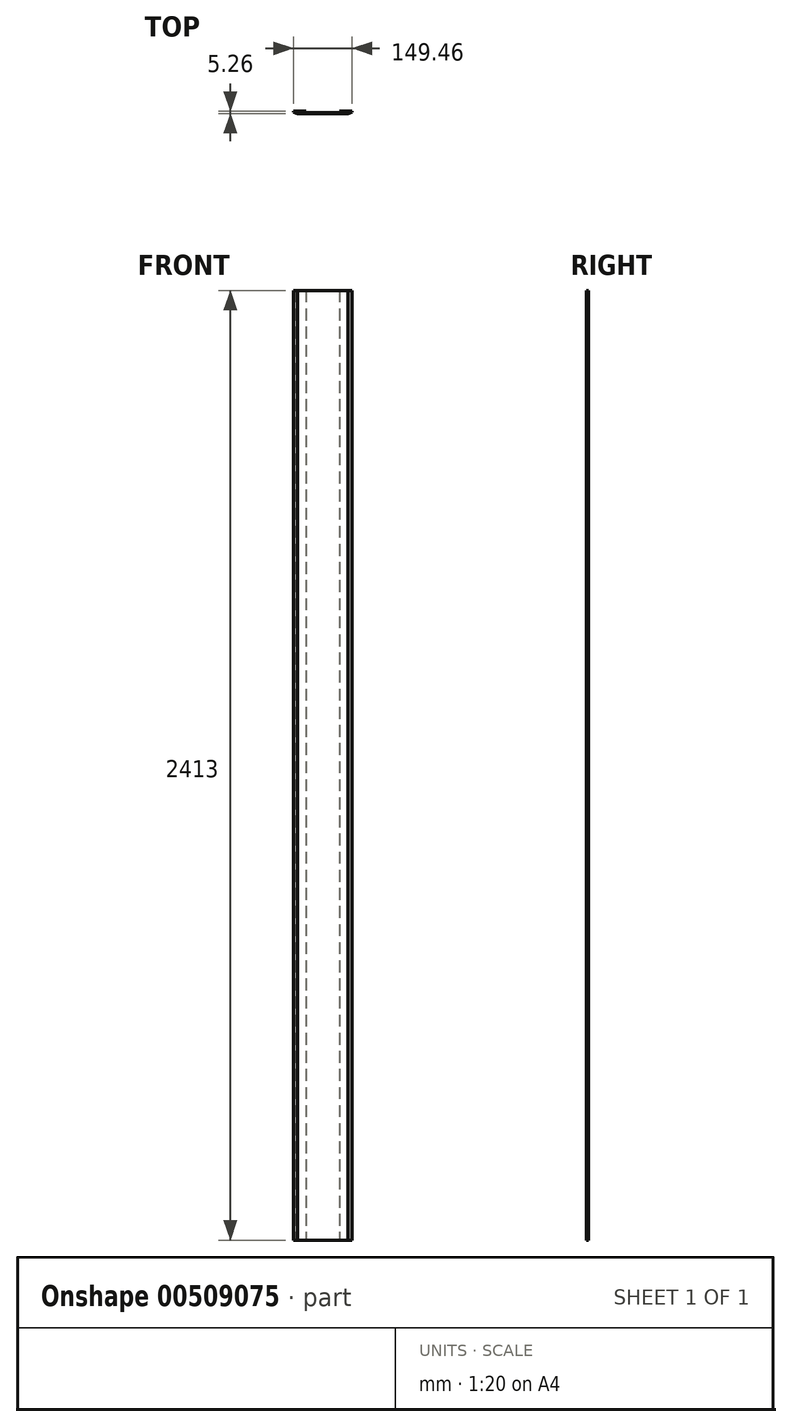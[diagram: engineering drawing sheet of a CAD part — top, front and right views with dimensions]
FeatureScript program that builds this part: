
annotation { "Feature Type Name" : "Feature", "Feature Type Description" : "" }
export const myFeature = defineFeature(function(context is Context, id is Id, definition is map)
    precondition{}
    {
        {
            var Q0;
            Q0=qCreatedBy(makeId("Top.planeOp"),FACE);
            var sketch = newSketch(context, id + "F0", { "sketchPlane" : qUnion([Q0])});
            skLineSegment(sketch, "E0", {"start": v(-431.8, -558.8) * mm, "end": v(431.8, -558.8) * mm});
            skLineSegment(sketch, "E1", {"start": v(431.8, -558.8) * mm, "end": v(431.8, 558.8) * mm});
            skLineSegment(sketch, "E2", {"start": v(431.8, 558.8) * mm, "end": v(-431.8, 558.8) * mm});
            skLineSegment(sketch, "E3", {"start": v(-431.8, 558.8) * mm, "end": v(-431.8, -558.8) * mm});
            skLineSegment(sketch, "E4", {"start": v(-381, -504.83) * mm, "end": v(381, -504.83) * mm});
            skLineSegment(sketch, "E5", {"start": v(381, -504.83) * mm, "end": v(381, 504.83) * mm});
            skLineSegment(sketch, "E6", {"start": v(381, 504.83) * mm, "end": v(360.7, 504.83) * mm});
            skLineSegment(sketch, "E7", {"start": v(265.82, 504.83) * mm, "end": v(-381, 504.83) * mm});
            skLineSegment(sketch, "E8", {"start": v(-381, 504.83) * mm, "end": v(-381, -504.83) * mm});
            skLineSegment(sketch, "E9", {"start": v(-381, -403.23) * mm, "end": v(381, -403.23) * mm});
            skLineSegment(sketch, "E10", {"start": v(-152.4, -403.23) * mm, "end": v(-152.4, -504.83) * mm});
            skLineSegment(sketch, "E11", {"start": v(152.4, -403.23) * mm, "end": v(152.4, -504.83) * mm});
            skLineSegment(sketch, "E12", {"start": v(349.12, 503.33) * mm, "end": v(324.77, 544.8) * mm});
            skLineSegment(sketch, "E13", {"start": v(324.92, 525.17) * mm, "end": v(343.26, 493.25) * mm});
            skLineSegment(sketch, "E14", {"start": v(345.3, 496.77) * mm, "end": v(323.11, 534.57) * mm});
            skLineSegment(sketch, "E15", {"start": v(351.17, 506.85) * mm, "end": v(327.06, 548.5) * mm});
            skLineSegment(sketch, "E16", {"start": v(335.24, 486.66) * mm, "end": v(339.43, 486.66) * mm});
            skLineSegment(sketch, "E17", {"start": v(323.53, 514.34) * mm, "end": v(339.43, 486.66) * mm});
            skLineSegment(sketch, "E18", {"start": v(324.77, 544.8) * mm, "end": v(303.2, 507.27) * mm});
            skLineSegment(sketch, "E19", {"start": v(323.11, 534.57) * mm, "end": v(305.2, 503.47) * mm});
            skLineSegment(sketch, "E20", {"start": v(303.02, 548.5) * mm, "end": v(279.32, 507.27) * mm});
            skLineSegment(sketch, "E21", {"start": v(305.2, 503.47) * mm, "end": v(281.51, 503.47) * mm});
            skLineSegment(sketch, "E22", {"start": v(303.2, 507.27) * mm, "end": v(279.32, 507.27) * mm});
            skLineSegment(sketch, "E23", {"start": v(287.46, 493.17) * mm, "end": v(311.53, 493.17) * mm});
            skLineSegment(sketch, "E24", {"start": v(285.48, 496.6) * mm, "end": v(309, 496.6) * mm});
            skLineSegment(sketch, "E25", {"start": v(315.3, 486.66) * mm, "end": v(291.22, 486.66) * mm});
            skLineSegment(sketch, "E26", {"start": v(281.51, 503.47) * mm, "end": v(285.48, 496.6) * mm});
            skLineSegment(sketch, "E27", {"start": v(287.46, 493.17) * mm, "end": v(291.22, 486.66) * mm});
            skLineSegment(sketch, "E28", {"start": v(309, 496.6) * mm, "end": v(324.92, 525.17) * mm});
            skLineSegment(sketch, "E29", {"start": v(311.53, 493.17) * mm, "end": v(323.53, 514.34) * mm});
            skLineSegment(sketch, "E30", {"start": v(325.28, 503.65) * mm, "end": v(315.3, 486.66) * mm});
            skLineSegment(sketch, "E31", {"start": v(319.7, 486.66) * mm, "end": v(326.89, 486.66) * mm});
            skLineSegment(sketch, "E32", {"start": v(319.7, 486.66) * mm, "end": v(323.3, 492.99) * mm});
            skLineSegment(sketch, "E33", {"start": v(335.24, 486.66) * mm, "end": v(325.28, 503.65) * mm});
            skLineSegment(sketch, "E34", {"start": v(323.3, 492.99) * mm, "end": v(326.89, 486.66) * mm});
            skLineSegment(sketch, "E35", {"start": v(327.06, 548.5) * mm, "end": v(303.02, 548.5) * mm});
            skLineSegment(sketch, "E36", {"start": v(343.26, 493.25) * mm, "end": v(345.3, 496.77) * mm});
            skLineSegment(sketch, "E37", {"start": v(349.12, 503.33) * mm, "end": v(351.17, 506.85) * mm});
            skCircle(sketch, "E38", {"center": v(350.6, 458.79) * mm, "radius": 1.85 * mm});
            skLineSegment(sketch, "E39", {"start": v(-201.65, 389.86) * mm, "end": v(-204.7, 389.86) * mm});
            skLineSegment(sketch, "E40", {"start": v(-201.65, 287.56) * mm, "end": v(-204.7, 287.56) * mm});
            skLineSegment(sketch, "E41", {"start": v(-204.7, 389.86) * mm, "end": v(-204.7, 405.1) * mm});
            skLineSegment(sketch, "E42", {"start": v(-201.65, 389.86) * mm, "end": v(-201.65, 405.1) * mm});
            skArc(sketch, "E43", {"start": v(-200.89, 405.86) * mm, "mid": v(-201.43, 405.64) * mm, "end": v(-201.65, 405.1) * mm});
            skArc(sketch, "E44", {"start": v(-200.89, 408.9) * mm, "mid": v(-203.58, 407.8) * mm, "end": v(-204.7, 405.1) * mm});
            skLineSegment(sketch, "E45", {"start": v(-200.89, 408.9) * mm, "end": v(-151.83, 408.9) * mm});
            skLineSegment(sketch, "E46", {"start": v(-200.89, 405.86) * mm, "end": v(-151.83, 405.86) * mm});
            skArc(sketch, "E47", {"start": v(-151.07, 405.1) * mm, "mid": v(-151.3, 405.64) * mm, "end": v(-151.83, 405.86) * mm});
            skArc(sketch, "E48", {"start": v(-148.02, 405.1) * mm, "mid": v(-149.14, 407.8) * mm, "end": v(-151.83, 408.9) * mm});
            skLineSegment(sketch, "E49", {"start": v(-148.02, 405.1) * mm, "end": v(-148.02, 272.32) * mm});
            skLineSegment(sketch, "E50", {"start": v(-151.07, 405.1) * mm, "end": v(-151.07, 272.32) * mm});
            skLineSegment(sketch, "E51", {"start": v(-204.7, 287.56) * mm, "end": v(-204.7, 273.15) * mm});
            skLineSegment(sketch, "E52", {"start": v(-201.65, 287.56) * mm, "end": v(-201.65, 273.15) * mm});
            skLineSegment(sketch, "E53", {"start": v(-200.06, 268.51) * mm, "end": v(-151.83, 268.51) * mm});
            skLineSegment(sketch, "E54", {"start": v(-200.06, 271.56) * mm, "end": v(-151.83, 271.56) * mm});
            skArc(sketch, "E55", {"start": v(-151.83, 271.56) * mm, "mid": v(-151.3, 271.79) * mm, "end": v(-151.07, 272.32) * mm});
            skArc(sketch, "E56", {"start": v(-151.83, 268.51) * mm, "mid": v(-149.14, 269.63) * mm, "end": v(-148.02, 272.32) * mm});
            skArc(sketch, "E57", {"start": v(-201.65, 273.15) * mm, "mid": v(-201.19, 272.03) * mm, "end": v(-200.06, 271.56) * mm});
            skArc(sketch, "E58", {"start": v(-204.7, 273.15) * mm, "mid": v(-203.34, 269.87) * mm, "end": v(-200.06, 268.51) * mm});
            skLineSegment(sketch, "E59", {"start": v(268.24, 192.18) * mm, "end": v(-275.4, 192.18) * mm});
            skLineSegment(sketch, "E60", {"start": v(-275.4, 267.58) * mm, "end": v(268.24, 267.58) * mm});
            skLineSegment(sketch, "E61", {"start": v(-275.4, 191.38) * mm, "end": v(268.24, 191.38) * mm});
            skLineSegment(sketch, "E62", {"start": v(-275.4, 189.56) * mm, "end": v(-275.4, 233.5) * mm});
            skLineSegment(sketch, "E63", {"start": v(-275.4, 238.46) * mm, "end": v(-275.4, 270.12) * mm});
            skLineSegment(sketch, "E64", {"start": v(-275.4, 233.5) * mm, "end": v(-264.27, 236) * mm});
            skLineSegment(sketch, "E65", {"start": v(-287.59, 236) * mm, "end": v(-275.4, 238.46) * mm});
            skLineSegment(sketch, "E66", {"start": v(-287.59, 236) * mm, "end": v(-264.27, 236) * mm});
            skLineSegment(sketch, "E67", {"start": v(268.24, 189.56) * mm, "end": v(268.24, 233.5) * mm});
            skLineSegment(sketch, "E68", {"start": v(268.24, 238.46) * mm, "end": v(268.24, 270.12) * mm});
            skLineSegment(sketch, "E69", {"start": v(268.24, 233.5) * mm, "end": v(279.38, 236) * mm});
            skLineSegment(sketch, "E70", {"start": v(256.06, 236) * mm, "end": v(268.24, 238.46) * mm});
            skLineSegment(sketch, "E71", {"start": v(256.06, 236) * mm, "end": v(279.38, 236) * mm});
            skLineSegment(sketch, "E72", {"start": v(267.92, 175.66) * mm, "end": v(267.92, 187.92) * mm});
            skLineSegment(sketch, "E73", {"start": v(-275.4, 175.66) * mm, "end": v(-275.4, 187.92) * mm});
            skLineSegment(sketch, "E74", {"start": v(131.2, 389.86) * mm, "end": v(128.15, 389.86) * mm});
            skLineSegment(sketch, "E75", {"start": v(131.2, 287.54) * mm, "end": v(128.15, 287.54) * mm});
            skLineSegment(sketch, "E76", {"start": v(128.15, 389.86) * mm, "end": v(128.15, 405.1) * mm});
            skLineSegment(sketch, "E77", {"start": v(131.2, 389.86) * mm, "end": v(131.2, 405.1) * mm});
            skArc(sketch, "E78", {"start": v(131.96, 408.9) * mm, "mid": v(129.27, 407.8) * mm, "end": v(128.15, 405.1) * mm});
            skLineSegment(sketch, "E79", {"start": v(131.96, 408.9) * mm, "end": v(182.96, 408.9) * mm});
            skLineSegment(sketch, "E80", {"start": v(131.96, 405.86) * mm, "end": v(182.96, 405.86) * mm});
            skArc(sketch, "E81", {"start": v(183.72, 405.1) * mm, "mid": v(183.5, 405.64) * mm, "end": v(182.96, 405.86) * mm});
            skArc(sketch, "E82", {"start": v(186.77, 405.1) * mm, "mid": v(185.65, 407.8) * mm, "end": v(182.96, 408.9) * mm});
            skLineSegment(sketch, "E83", {"start": v(186.77, 405.1) * mm, "end": v(186.77, 272.3) * mm});
            skLineSegment(sketch, "E84", {"start": v(183.72, 405.1) * mm, "end": v(183.72, 272.3) * mm});
            skLineSegment(sketch, "E85", {"start": v(128.15, 287.54) * mm, "end": v(128.15, 273.12) * mm});
            skLineSegment(sketch, "E86", {"start": v(131.2, 287.54) * mm, "end": v(131.2, 273.12) * mm});
            skLineSegment(sketch, "E87", {"start": v(132.79, 268.49) * mm, "end": v(182.96, 268.49) * mm});
            skLineSegment(sketch, "E88", {"start": v(132.79, 271.53) * mm, "end": v(182.96, 271.53) * mm});
            skArc(sketch, "E89", {"start": v(182.96, 271.53) * mm, "mid": v(183.5, 271.76) * mm, "end": v(183.72, 272.3) * mm});
            skArc(sketch, "E90", {"start": v(182.96, 268.49) * mm, "mid": v(185.65, 269.6) * mm, "end": v(186.77, 272.3) * mm});
            skArc(sketch, "E91", {"start": v(131.2, 273.12) * mm, "mid": v(131.67, 272) * mm, "end": v(132.79, 271.53) * mm});
            skArc(sketch, "E92", {"start": v(128.15, 273.12) * mm, "mid": v(129.51, 269.84) * mm, "end": v(132.79, 268.49) * mm});
            skLineSegment(sketch, "E93", {"start": v(-275.4, 266.78) * mm, "end": v(268.24, 266.78) * mm});
            skArc(sketch, "E94", {"start": v(131.96, 405.86) * mm, "mid": v(131.42, 405.64) * mm, "end": v(131.2, 405.1) * mm});
            skLineSegment(sketch, "E95", {"start": v(-148.02, 350.55) * mm, "end": v(-147.38, 350.55) * mm});
            skLineSegment(sketch, "E96", {"start": v(268.24, 220.63) * mm, "end": v(-275.4, 220.63) * mm});
            skLineSegment(sketch, "E97", {"start": v(-275.4, 219.83) * mm, "end": v(268.24, 219.83) * mm});
            skLineSegment(sketch, "E98", {"start": v(111.4, 219.88) * mm, "end": v(200.2, 219.88) * mm});
            skLineSegment(sketch, "E99", {"start": v(200.2, 219.88) * mm, "end": v(200.2, 218.1) * mm});
            skLineSegment(sketch, "E100", {"start": v(111.4, 219.88) * mm, "end": v(111.4, 218.1) * mm});
            skLineSegment(sketch, "E101", {"start": v(111.4, 218.1) * mm, "end": v(200.2, 218.1) * mm});
            skLineSegment(sketch, "E102", {"start": v(165.87, 216.24) * mm, "end": v(165.87, 217.5) * mm});
            skLineSegment(sketch, "E103", {"start": v(152.66, 216.24) * mm, "end": v(152.66, 217.5) * mm});
            skLineSegment(sketch, "E104", {"start": v(164.46, 211.81) * mm, "end": v(164.46, 216.24) * mm});
            skLineSegment(sketch, "E105", {"start": v(154.07, 211.81) * mm, "end": v(154.07, 216.24) * mm});
            skLineSegment(sketch, "E106", {"start": v(161.7, 259.32) * mm, "end": v(161.7, 260.34) * mm});
            skLineSegment(sketch, "E107", {"start": v(161.7, 261.14) * mm, "end": v(161.7, 262.16) * mm});
            skLineSegment(sketch, "E108", {"start": v(161.7, 262.95) * mm, "end": v(161.7, 263.97) * mm});
            skLineSegment(sketch, "E109", {"start": v(161.7, 264.76) * mm, "end": v(161.7, 265.78) * mm});
            skLineSegment(sketch, "E110", {"start": v(161.7, 266.58) * mm, "end": v(161.7, 267.6) * mm});
            skLineSegment(sketch, "E111", {"start": v(161.7, 268.39) * mm, "end": v(161.7, 269.41) * mm});
            skLineSegment(sketch, "E112", {"start": v(161.7, 270.2) * mm, "end": v(161.7, 271.22) * mm});
            skLineSegment(sketch, "E113", {"start": v(161.7, 272.02) * mm, "end": v(161.7, 273.04) * mm});
            skLineSegment(sketch, "E114", {"start": v(161.7, 273.83) * mm, "end": v(161.7, 274.85) * mm});
            skLineSegment(sketch, "E115", {"start": v(161.7, 275.64) * mm, "end": v(161.7, 276.67) * mm});
            skLineSegment(sketch, "E116", {"start": v(161.7, 277.46) * mm, "end": v(161.7, 278.48) * mm});
            skLineSegment(sketch, "E117", {"start": v(156.83, 257.5) * mm, "end": v(156.83, 258.53) * mm});
            skLineSegment(sketch, "E118", {"start": v(156.83, 259.32) * mm, "end": v(156.83, 260.34) * mm});
            skLineSegment(sketch, "E119", {"start": v(156.83, 261.14) * mm, "end": v(156.83, 262.16) * mm});
            skLineSegment(sketch, "E120", {"start": v(156.83, 262.95) * mm, "end": v(156.83, 263.97) * mm});
            skLineSegment(sketch, "E121", {"start": v(156.83, 264.76) * mm, "end": v(156.83, 265.78) * mm});
            skLineSegment(sketch, "E122", {"start": v(156.83, 266.58) * mm, "end": v(156.83, 267.6) * mm});
            skLineSegment(sketch, "E123", {"start": v(156.83, 268.39) * mm, "end": v(156.83, 269.41) * mm});
            skLineSegment(sketch, "E124", {"start": v(156.83, 270.2) * mm, "end": v(156.83, 271.22) * mm});
            skLineSegment(sketch, "E125", {"start": v(156.83, 272.02) * mm, "end": v(156.83, 273.04) * mm});
            skLineSegment(sketch, "E126", {"start": v(156.83, 273.83) * mm, "end": v(156.83, 274.85) * mm});
            skLineSegment(sketch, "E127", {"start": v(156.83, 275.64) * mm, "end": v(156.83, 276.67) * mm});
            skLineSegment(sketch, "E128", {"start": v(156.14, 258.93) * mm, "end": v(156.83, 258.53) * mm});
            skLineSegment(sketch, "E129", {"start": v(156.14, 258.93) * mm, "end": v(156.83, 259.32) * mm});
            skLineSegment(sketch, "E130", {"start": v(156.14, 260.74) * mm, "end": v(156.83, 260.34) * mm});
            skLineSegment(sketch, "E131", {"start": v(156.14, 260.74) * mm, "end": v(156.83, 261.14) * mm});
            skLineSegment(sketch, "E132", {"start": v(162.39, 260.74) * mm, "end": v(161.7, 260.34) * mm});
            skLineSegment(sketch, "E133", {"start": v(162.39, 260.74) * mm, "end": v(161.7, 261.14) * mm});
            skLineSegment(sketch, "E134", {"start": v(162.39, 262.55) * mm, "end": v(161.7, 262.16) * mm});
            skLineSegment(sketch, "E135", {"start": v(162.39, 262.55) * mm, "end": v(161.7, 262.95) * mm});
            skLineSegment(sketch, "E136", {"start": v(156.14, 258.93) * mm, "end": v(162.39, 260.74) * mm});
            skLineSegment(sketch, "E137", {"start": v(156.14, 260.74) * mm, "end": v(162.39, 262.55) * mm});
            skLineSegment(sketch, "E138", {"start": v(156.83, 258.53) * mm, "end": v(161.7, 260.34) * mm});
            skLineSegment(sketch, "E139", {"start": v(156.83, 259.32) * mm, "end": v(161.7, 261.14) * mm});
            skLineSegment(sketch, "E140", {"start": v(156.83, 260.34) * mm, "end": v(161.7, 262.16) * mm});
            skLineSegment(sketch, "E141", {"start": v(156.83, 261.14) * mm, "end": v(161.7, 262.95) * mm});
            skLineSegment(sketch, "E142", {"start": v(156.14, 262.55) * mm, "end": v(156.83, 262.16) * mm});
            skLineSegment(sketch, "E143", {"start": v(156.14, 262.55) * mm, "end": v(156.83, 262.95) * mm});
            skLineSegment(sketch, "E144", {"start": v(156.14, 264.37) * mm, "end": v(156.83, 263.97) * mm});
            skLineSegment(sketch, "E145", {"start": v(156.14, 264.37) * mm, "end": v(156.83, 264.76) * mm});
            skLineSegment(sketch, "E146", {"start": v(162.39, 264.37) * mm, "end": v(161.7, 263.97) * mm});
            skLineSegment(sketch, "E147", {"start": v(162.39, 264.37) * mm, "end": v(161.7, 264.76) * mm});
            skLineSegment(sketch, "E148", {"start": v(162.39, 266.18) * mm, "end": v(161.7, 265.78) * mm});
            skLineSegment(sketch, "E149", {"start": v(162.39, 266.18) * mm, "end": v(161.7, 266.58) * mm});
            skLineSegment(sketch, "E150", {"start": v(156.14, 262.55) * mm, "end": v(162.39, 264.37) * mm});
            skLineSegment(sketch, "E151", {"start": v(156.14, 264.37) * mm, "end": v(162.39, 266.18) * mm});
            skLineSegment(sketch, "E152", {"start": v(156.83, 262.16) * mm, "end": v(161.7, 263.97) * mm});
            skLineSegment(sketch, "E153", {"start": v(156.83, 262.95) * mm, "end": v(161.7, 264.76) * mm});
            skLineSegment(sketch, "E154", {"start": v(156.83, 263.97) * mm, "end": v(161.7, 265.78) * mm});
            skLineSegment(sketch, "E155", {"start": v(156.83, 264.76) * mm, "end": v(161.7, 266.58) * mm});
            skLineSegment(sketch, "E156", {"start": v(156.14, 266.18) * mm, "end": v(156.83, 265.78) * mm});
            skLineSegment(sketch, "E157", {"start": v(156.14, 266.18) * mm, "end": v(156.83, 266.58) * mm});
            skLineSegment(sketch, "E158", {"start": v(162.39, 268) * mm, "end": v(161.7, 267.6) * mm});
            skLineSegment(sketch, "E159", {"start": v(162.39, 268) * mm, "end": v(161.7, 268.39) * mm});
            skLineSegment(sketch, "E160", {"start": v(156.14, 266.18) * mm, "end": v(162.39, 268) * mm});
            skLineSegment(sketch, "E161", {"start": v(156.83, 265.78) * mm, "end": v(161.7, 267.6) * mm});
            skLineSegment(sketch, "E162", {"start": v(156.83, 266.58) * mm, "end": v(161.7, 268.39) * mm});
            skLineSegment(sketch, "E163", {"start": v(156.14, 268) * mm, "end": v(156.83, 267.6) * mm});
            skLineSegment(sketch, "E164", {"start": v(156.14, 268) * mm, "end": v(156.83, 268.39) * mm});
            skLineSegment(sketch, "E165", {"start": v(156.14, 269.8) * mm, "end": v(156.83, 269.41) * mm});
            skLineSegment(sketch, "E166", {"start": v(156.14, 269.8) * mm, "end": v(156.83, 270.2) * mm});
            skLineSegment(sketch, "E167", {"start": v(162.39, 269.8) * mm, "end": v(161.7, 269.41) * mm});
            skLineSegment(sketch, "E168", {"start": v(162.39, 269.8) * mm, "end": v(161.7, 270.2) * mm});
            skLineSegment(sketch, "E169", {"start": v(162.39, 271.62) * mm, "end": v(161.7, 271.22) * mm});
            skLineSegment(sketch, "E170", {"start": v(162.39, 271.62) * mm, "end": v(161.7, 272.02) * mm});
            skLineSegment(sketch, "E171", {"start": v(156.14, 268) * mm, "end": v(162.39, 269.8) * mm});
            skLineSegment(sketch, "E172", {"start": v(156.14, 269.8) * mm, "end": v(162.39, 271.62) * mm});
            skLineSegment(sketch, "E173", {"start": v(156.83, 267.6) * mm, "end": v(161.7, 269.41) * mm});
            skLineSegment(sketch, "E174", {"start": v(156.83, 268.39) * mm, "end": v(161.7, 270.2) * mm});
            skLineSegment(sketch, "E175", {"start": v(156.83, 269.41) * mm, "end": v(161.7, 271.22) * mm});
            skLineSegment(sketch, "E176", {"start": v(156.83, 270.2) * mm, "end": v(161.7, 272.02) * mm});
            skLineSegment(sketch, "E177", {"start": v(156.14, 271.62) * mm, "end": v(156.83, 271.22) * mm});
            skLineSegment(sketch, "E178", {"start": v(156.14, 271.62) * mm, "end": v(156.83, 272.02) * mm});
            skLineSegment(sketch, "E179", {"start": v(156.14, 273.43) * mm, "end": v(156.83, 273.04) * mm});
            skLineSegment(sketch, "E180", {"start": v(156.14, 273.43) * mm, "end": v(156.83, 273.83) * mm});
            skLineSegment(sketch, "E181", {"start": v(162.39, 273.43) * mm, "end": v(161.7, 273.04) * mm});
            skLineSegment(sketch, "E182", {"start": v(162.39, 273.43) * mm, "end": v(161.7, 273.83) * mm});
            skLineSegment(sketch, "E183", {"start": v(162.39, 275.25) * mm, "end": v(161.7, 274.85) * mm});
            skLineSegment(sketch, "E184", {"start": v(162.39, 275.25) * mm, "end": v(161.7, 275.64) * mm});
            skLineSegment(sketch, "E185", {"start": v(156.14, 271.62) * mm, "end": v(162.39, 273.43) * mm});
            skLineSegment(sketch, "E186", {"start": v(156.14, 273.43) * mm, "end": v(162.39, 275.25) * mm});
            skLineSegment(sketch, "E187", {"start": v(156.83, 271.22) * mm, "end": v(161.7, 273.04) * mm});
            skLineSegment(sketch, "E188", {"start": v(156.83, 272.02) * mm, "end": v(161.7, 273.83) * mm});
            skLineSegment(sketch, "E189", {"start": v(156.83, 273.04) * mm, "end": v(161.7, 274.85) * mm});
            skLineSegment(sketch, "E190", {"start": v(156.83, 273.83) * mm, "end": v(161.7, 275.64) * mm});
            skLineSegment(sketch, "E191", {"start": v(156.14, 275.25) * mm, "end": v(156.83, 274.85) * mm});
            skLineSegment(sketch, "E192", {"start": v(156.14, 275.25) * mm, "end": v(156.83, 275.64) * mm});
            skLineSegment(sketch, "E193", {"start": v(156.14, 277.06) * mm, "end": v(156.83, 276.67) * mm});
            skLineSegment(sketch, "E194", {"start": v(156.14, 277.06) * mm, "end": v(156.83, 277.46) * mm});
            skLineSegment(sketch, "E195", {"start": v(162.39, 277.06) * mm, "end": v(161.7, 276.67) * mm});
            skLineSegment(sketch, "E196", {"start": v(162.39, 277.06) * mm, "end": v(161.7, 277.46) * mm});
            skLineSegment(sketch, "E197", {"start": v(162.39, 278.87) * mm, "end": v(161.7, 278.48) * mm});
            skLineSegment(sketch, "E198", {"start": v(162.39, 278.87) * mm, "end": v(161.7, 279.27) * mm});
            skLineSegment(sketch, "E199", {"start": v(156.14, 275.25) * mm, "end": v(162.39, 277.06) * mm});
            skLineSegment(sketch, "E200", {"start": v(156.14, 277.06) * mm, "end": v(162.39, 278.87) * mm});
            skLineSegment(sketch, "E201", {"start": v(156.83, 274.85) * mm, "end": v(161.7, 276.67) * mm});
            skLineSegment(sketch, "E202", {"start": v(156.83, 275.64) * mm, "end": v(161.7, 277.46) * mm});
            skLineSegment(sketch, "E203", {"start": v(156.83, 276.67) * mm, "end": v(161.7, 278.48) * mm});
            skLineSegment(sketch, "E204", {"start": v(156.83, 277.46) * mm, "end": v(161.7, 279.27) * mm});
            skLineSegment(sketch, "E205", {"start": v(152.66, 217.5) * mm, "end": v(165.87, 217.5) * mm});
            skLineSegment(sketch, "E206", {"start": v(152.66, 216.24) * mm, "end": v(165.87, 216.24) * mm});
            skLineSegment(sketch, "E207", {"start": v(154.77, 211.41) * mm, "end": v(163.76, 211.41) * mm});
            skLineSegment(sketch, "E208", {"start": v(156.67, 211.81) * mm, "end": v(156.67, 216.24) * mm});
            skLineSegment(sketch, "E209", {"start": v(161.86, 211.81) * mm, "end": v(161.86, 216.24) * mm});
            skLineSegment(sketch, "E210", {"start": v(154.77, 211.41) * mm, "end": v(154.07, 211.81) * mm});
            skLineSegment(sketch, "E211", {"start": v(163.76, 211.41) * mm, "end": v(164.46, 211.81) * mm});
            skLineSegment(sketch, "E212", {"start": v(161.16, 211.41) * mm, "end": v(161.86, 211.81) * mm});
            skLineSegment(sketch, "E213", {"start": v(155.97, 211.41) * mm, "end": v(156.67, 211.81) * mm});
            skLineSegment(sketch, "E214", {"start": v(162.56, 211.41) * mm, "end": v(161.86, 211.81) * mm});
            skLineSegment(sketch, "E215", {"start": v(157.36, 211.41) * mm, "end": v(156.67, 211.81) * mm});
            skLineSegment(sketch, "E216", {"start": v(156.83, 277.46) * mm, "end": v(156.83, 288.94) * mm});
            skLineSegment(sketch, "E217", {"start": v(161.05, 279.03) * mm, "end": v(161.05, 288.94) * mm});
            skLineSegment(sketch, "E218", {"start": v(158.94, 290.16) * mm, "end": v(156.83, 288.94) * mm});
            skLineSegment(sketch, "E219", {"start": v(158.94, 290.16) * mm, "end": v(161.05, 288.94) * mm});
            skLineSegment(sketch, "E220", {"start": v(158.94, 290.16) * mm, "end": v(158.94, 280.63) * mm});
            skArc(sketch, "E221", {"start": v(158.94, 280.63) * mm, "mid": v(159.28, 279.49) * mm, "end": v(160.18, 278.7) * mm});
            skLineSegment(sketch, "E222", {"start": v(156.14, 257.11) * mm, "end": v(156.83, 256.72) * mm});
            skLineSegment(sketch, "E223", {"start": v(156.14, 257.11) * mm, "end": v(156.83, 257.5) * mm});
            skLineSegment(sketch, "E224", {"start": v(162.39, 258.93) * mm, "end": v(161.7, 258.53) * mm});
            skLineSegment(sketch, "E225", {"start": v(162.39, 258.93) * mm, "end": v(161.7, 259.32) * mm});
            skLineSegment(sketch, "E226", {"start": v(156.14, 257.11) * mm, "end": v(162.39, 258.93) * mm});
            skLineSegment(sketch, "E227", {"start": v(156.83, 256.72) * mm, "end": v(161.7, 258.53) * mm});
            skLineSegment(sketch, "E228", {"start": v(156.83, 257.5) * mm, "end": v(161.7, 259.32) * mm});
            skLineSegment(sketch, "E229", {"start": v(156.83, 256.72) * mm, "end": v(156.83, 217.5) * mm});
            skLineSegment(sketch, "E230", {"start": v(161.7, 258.53) * mm, "end": v(161.7, 217.5) * mm});
            skLineSegment(sketch, "E231", {"start": v(-224.84, 219.88) * mm, "end": v(-136.05, 219.88) * mm});
            skLineSegment(sketch, "E232", {"start": v(-224.84, 218.1) * mm, "end": v(-136.05, 218.1) * mm});
            skLineSegment(sketch, "E233", {"start": v(-136.05, 219.88) * mm, "end": v(-136.05, 218.1) * mm});
            skLineSegment(sketch, "E234", {"start": v(-224.84, 219.88) * mm, "end": v(-224.84, 218.1) * mm});
            skLineSegment(sketch, "E235", {"start": v(-170.37, 216.24) * mm, "end": v(-170.37, 217.5) * mm});
            skLineSegment(sketch, "E236", {"start": v(-183.58, 216.24) * mm, "end": v(-183.58, 217.5) * mm});
            skLineSegment(sketch, "E237", {"start": v(-171.78, 211.81) * mm, "end": v(-171.78, 216.24) * mm});
            skLineSegment(sketch, "E238", {"start": v(-182.17, 211.81) * mm, "end": v(-182.17, 216.24) * mm});
            skLineSegment(sketch, "E239", {"start": v(-174.54, 259.32) * mm, "end": v(-174.54, 260.34) * mm});
            skLineSegment(sketch, "E240", {"start": v(-174.54, 261.14) * mm, "end": v(-174.54, 262.16) * mm});
            skLineSegment(sketch, "E241", {"start": v(-174.54, 262.95) * mm, "end": v(-174.54, 263.97) * mm});
            skLineSegment(sketch, "E242", {"start": v(-174.54, 264.76) * mm, "end": v(-174.54, 265.78) * mm});
            skLineSegment(sketch, "E243", {"start": v(-174.54, 266.58) * mm, "end": v(-174.54, 267.6) * mm});
            skLineSegment(sketch, "E244", {"start": v(-174.54, 268.39) * mm, "end": v(-174.54, 269.41) * mm});
            skLineSegment(sketch, "E245", {"start": v(-174.54, 270.2) * mm, "end": v(-174.54, 271.22) * mm});
            skLineSegment(sketch, "E246", {"start": v(-174.54, 272.02) * mm, "end": v(-174.54, 273.04) * mm});
            skLineSegment(sketch, "E247", {"start": v(-174.54, 273.83) * mm, "end": v(-174.54, 274.85) * mm});
            skLineSegment(sketch, "E248", {"start": v(-174.54, 275.64) * mm, "end": v(-174.54, 276.67) * mm});
            skLineSegment(sketch, "E249", {"start": v(-174.54, 277.46) * mm, "end": v(-174.54, 278.48) * mm});
            skLineSegment(sketch, "E250", {"start": v(-179.41, 257.5) * mm, "end": v(-179.41, 258.53) * mm});
            skLineSegment(sketch, "E251", {"start": v(-179.41, 259.32) * mm, "end": v(-179.41, 260.34) * mm});
            skLineSegment(sketch, "E252", {"start": v(-179.41, 261.14) * mm, "end": v(-179.41, 262.16) * mm});
            skLineSegment(sketch, "E253", {"start": v(-179.41, 262.95) * mm, "end": v(-179.41, 263.97) * mm});
            skLineSegment(sketch, "E254", {"start": v(-179.41, 264.76) * mm, "end": v(-179.41, 265.78) * mm});
            skLineSegment(sketch, "E255", {"start": v(-179.41, 266.58) * mm, "end": v(-179.41, 267.6) * mm});
            skLineSegment(sketch, "E256", {"start": v(-179.41, 268.39) * mm, "end": v(-179.41, 269.41) * mm});
            skLineSegment(sketch, "E257", {"start": v(-179.41, 270.2) * mm, "end": v(-179.41, 271.22) * mm});
            skLineSegment(sketch, "E258", {"start": v(-179.41, 272.02) * mm, "end": v(-179.41, 273.04) * mm});
            skLineSegment(sketch, "E259", {"start": v(-179.41, 273.83) * mm, "end": v(-179.41, 274.85) * mm});
            skLineSegment(sketch, "E260", {"start": v(-179.41, 275.64) * mm, "end": v(-179.41, 276.67) * mm});
            skLineSegment(sketch, "E261", {"start": v(-180.1, 258.93) * mm, "end": v(-179.41, 258.53) * mm});
            skLineSegment(sketch, "E262", {"start": v(-180.1, 258.93) * mm, "end": v(-179.41, 259.32) * mm});
            skLineSegment(sketch, "E263", {"start": v(-180.1, 260.74) * mm, "end": v(-179.41, 260.34) * mm});
            skLineSegment(sketch, "E264", {"start": v(-180.1, 260.74) * mm, "end": v(-179.41, 261.14) * mm});
            skLineSegment(sketch, "E265", {"start": v(-173.85, 260.74) * mm, "end": v(-174.54, 260.34) * mm});
            skLineSegment(sketch, "E266", {"start": v(-173.85, 260.74) * mm, "end": v(-174.54, 261.14) * mm});
            skLineSegment(sketch, "E267", {"start": v(-173.85, 262.55) * mm, "end": v(-174.54, 262.16) * mm});
            skLineSegment(sketch, "E268", {"start": v(-173.85, 262.55) * mm, "end": v(-174.54, 262.95) * mm});
            skLineSegment(sketch, "E269", {"start": v(-180.1, 258.93) * mm, "end": v(-173.85, 260.74) * mm});
            skLineSegment(sketch, "E270", {"start": v(-180.1, 260.74) * mm, "end": v(-173.85, 262.55) * mm});
            skLineSegment(sketch, "E271", {"start": v(-179.41, 258.53) * mm, "end": v(-174.54, 260.34) * mm});
            skLineSegment(sketch, "E272", {"start": v(-179.41, 259.32) * mm, "end": v(-174.54, 261.14) * mm});
            skLineSegment(sketch, "E273", {"start": v(-179.41, 260.34) * mm, "end": v(-174.54, 262.16) * mm});
            skLineSegment(sketch, "E274", {"start": v(-179.41, 261.14) * mm, "end": v(-174.54, 262.95) * mm});
            skLineSegment(sketch, "E275", {"start": v(-180.1, 262.55) * mm, "end": v(-179.41, 262.16) * mm});
            skLineSegment(sketch, "E276", {"start": v(-180.1, 262.55) * mm, "end": v(-179.41, 262.95) * mm});
            skLineSegment(sketch, "E277", {"start": v(-180.1, 264.37) * mm, "end": v(-179.41, 263.97) * mm});
            skLineSegment(sketch, "E278", {"start": v(-180.1, 264.37) * mm, "end": v(-179.41, 264.76) * mm});
            skLineSegment(sketch, "E279", {"start": v(-173.85, 264.37) * mm, "end": v(-174.54, 263.97) * mm});
            skLineSegment(sketch, "E280", {"start": v(-173.85, 264.37) * mm, "end": v(-174.54, 264.76) * mm});
            skLineSegment(sketch, "E281", {"start": v(-173.85, 266.18) * mm, "end": v(-174.54, 265.78) * mm});
            skLineSegment(sketch, "E282", {"start": v(-173.85, 266.18) * mm, "end": v(-174.54, 266.58) * mm});
            skLineSegment(sketch, "E283", {"start": v(-180.1, 262.55) * mm, "end": v(-173.85, 264.37) * mm});
            skLineSegment(sketch, "E284", {"start": v(-180.1, 264.37) * mm, "end": v(-173.85, 266.18) * mm});
            skLineSegment(sketch, "E285", {"start": v(-179.41, 262.16) * mm, "end": v(-174.54, 263.97) * mm});
            skLineSegment(sketch, "E286", {"start": v(-179.41, 262.95) * mm, "end": v(-174.54, 264.76) * mm});
            skLineSegment(sketch, "E287", {"start": v(-179.41, 263.97) * mm, "end": v(-174.54, 265.78) * mm});
            skLineSegment(sketch, "E288", {"start": v(-179.41, 264.76) * mm, "end": v(-174.54, 266.58) * mm});
            skLineSegment(sketch, "E289", {"start": v(-180.1, 266.18) * mm, "end": v(-179.41, 265.78) * mm});
            skLineSegment(sketch, "E290", {"start": v(-180.1, 266.18) * mm, "end": v(-179.41, 266.58) * mm});
            skLineSegment(sketch, "E291", {"start": v(-173.85, 268) * mm, "end": v(-174.54, 267.6) * mm});
            skLineSegment(sketch, "E292", {"start": v(-173.85, 268) * mm, "end": v(-174.54, 268.39) * mm});
            skLineSegment(sketch, "E293", {"start": v(-180.1, 266.18) * mm, "end": v(-173.85, 268) * mm});
            skLineSegment(sketch, "E294", {"start": v(-179.41, 265.78) * mm, "end": v(-174.54, 267.6) * mm});
            skLineSegment(sketch, "E295", {"start": v(-179.41, 266.58) * mm, "end": v(-174.54, 268.39) * mm});
            skLineSegment(sketch, "E296", {"start": v(-180.1, 268) * mm, "end": v(-179.41, 267.6) * mm});
            skLineSegment(sketch, "E297", {"start": v(-180.1, 268) * mm, "end": v(-179.41, 268.39) * mm});
            skLineSegment(sketch, "E298", {"start": v(-180.1, 269.8) * mm, "end": v(-179.41, 269.41) * mm});
            skLineSegment(sketch, "E299", {"start": v(-180.1, 269.8) * mm, "end": v(-179.41, 270.2) * mm});
            skLineSegment(sketch, "E300", {"start": v(-173.85, 269.8) * mm, "end": v(-174.54, 269.41) * mm});
            skLineSegment(sketch, "E301", {"start": v(-173.85, 269.8) * mm, "end": v(-174.54, 270.2) * mm});
            skLineSegment(sketch, "E302", {"start": v(-173.85, 271.62) * mm, "end": v(-174.54, 271.22) * mm});
            skLineSegment(sketch, "E303", {"start": v(-173.85, 271.62) * mm, "end": v(-174.54, 272.02) * mm});
            skLineSegment(sketch, "E304", {"start": v(-180.1, 268) * mm, "end": v(-173.85, 269.8) * mm});
            skLineSegment(sketch, "E305", {"start": v(-180.1, 269.8) * mm, "end": v(-173.85, 271.62) * mm});
            skLineSegment(sketch, "E306", {"start": v(-179.41, 267.6) * mm, "end": v(-174.54, 269.41) * mm});
            skLineSegment(sketch, "E307", {"start": v(-179.41, 268.39) * mm, "end": v(-174.54, 270.2) * mm});
            skLineSegment(sketch, "E308", {"start": v(-179.41, 269.41) * mm, "end": v(-174.54, 271.22) * mm});
            skLineSegment(sketch, "E309", {"start": v(-179.41, 270.2) * mm, "end": v(-174.54, 272.02) * mm});
            skLineSegment(sketch, "E310", {"start": v(-180.1, 271.62) * mm, "end": v(-179.41, 271.22) * mm});
            skLineSegment(sketch, "E311", {"start": v(-180.1, 271.62) * mm, "end": v(-179.41, 272.02) * mm});
            skLineSegment(sketch, "E312", {"start": v(-180.1, 273.43) * mm, "end": v(-179.41, 273.04) * mm});
            skLineSegment(sketch, "E313", {"start": v(-180.1, 273.43) * mm, "end": v(-179.41, 273.83) * mm});
            skLineSegment(sketch, "E314", {"start": v(-173.85, 273.43) * mm, "end": v(-174.54, 273.04) * mm});
            skLineSegment(sketch, "E315", {"start": v(-173.85, 273.43) * mm, "end": v(-174.54, 273.83) * mm});
            skLineSegment(sketch, "E316", {"start": v(-173.85, 275.25) * mm, "end": v(-174.54, 274.85) * mm});
            skLineSegment(sketch, "E317", {"start": v(-173.85, 275.25) * mm, "end": v(-174.54, 275.64) * mm});
            skLineSegment(sketch, "E318", {"start": v(-180.1, 271.62) * mm, "end": v(-173.85, 273.43) * mm});
            skLineSegment(sketch, "E319", {"start": v(-180.1, 273.43) * mm, "end": v(-173.85, 275.25) * mm});
            skLineSegment(sketch, "E320", {"start": v(-179.41, 271.22) * mm, "end": v(-174.54, 273.04) * mm});
            skLineSegment(sketch, "E321", {"start": v(-179.41, 272.02) * mm, "end": v(-174.54, 273.83) * mm});
            skLineSegment(sketch, "E322", {"start": v(-179.41, 273.04) * mm, "end": v(-174.54, 274.85) * mm});
            skLineSegment(sketch, "E323", {"start": v(-179.41, 273.83) * mm, "end": v(-174.54, 275.64) * mm});
            skLineSegment(sketch, "E324", {"start": v(-180.1, 275.25) * mm, "end": v(-179.41, 274.85) * mm});
            skLineSegment(sketch, "E325", {"start": v(-180.1, 275.25) * mm, "end": v(-179.41, 275.64) * mm});
            skLineSegment(sketch, "E326", {"start": v(-180.1, 277.06) * mm, "end": v(-179.41, 276.67) * mm});
            skLineSegment(sketch, "E327", {"start": v(-180.1, 277.06) * mm, "end": v(-179.41, 277.46) * mm});
            skLineSegment(sketch, "E328", {"start": v(-173.85, 277.06) * mm, "end": v(-174.54, 276.67) * mm});
            skLineSegment(sketch, "E329", {"start": v(-173.85, 277.06) * mm, "end": v(-174.54, 277.46) * mm});
            skLineSegment(sketch, "E330", {"start": v(-173.85, 278.87) * mm, "end": v(-174.54, 278.48) * mm});
            skLineSegment(sketch, "E331", {"start": v(-173.85, 278.87) * mm, "end": v(-174.54, 279.27) * mm});
            skLineSegment(sketch, "E332", {"start": v(-180.1, 275.25) * mm, "end": v(-173.85, 277.06) * mm});
            skLineSegment(sketch, "E333", {"start": v(-180.1, 277.06) * mm, "end": v(-173.85, 278.87) * mm});
            skLineSegment(sketch, "E334", {"start": v(-179.41, 274.85) * mm, "end": v(-174.54, 276.67) * mm});
            skLineSegment(sketch, "E335", {"start": v(-179.41, 275.64) * mm, "end": v(-174.54, 277.46) * mm});
            skLineSegment(sketch, "E336", {"start": v(-179.41, 276.67) * mm, "end": v(-174.54, 278.48) * mm});
            skLineSegment(sketch, "E337", {"start": v(-179.41, 277.46) * mm, "end": v(-174.54, 279.27) * mm});
            skLineSegment(sketch, "E338", {"start": v(-183.58, 217.5) * mm, "end": v(-170.37, 217.5) * mm});
            skLineSegment(sketch, "E339", {"start": v(-183.58, 216.24) * mm, "end": v(-170.37, 216.24) * mm});
            skLineSegment(sketch, "E340", {"start": v(-181.47, 211.41) * mm, "end": v(-172.48, 211.41) * mm});
            skLineSegment(sketch, "E341", {"start": v(-179.57, 211.81) * mm, "end": v(-179.57, 216.24) * mm});
            skLineSegment(sketch, "E342", {"start": v(-174.38, 211.81) * mm, "end": v(-174.38, 216.24) * mm});
            skLineSegment(sketch, "E343", {"start": v(-181.47, 211.41) * mm, "end": v(-182.17, 211.81) * mm});
            skLineSegment(sketch, "E344", {"start": v(-172.48, 211.41) * mm, "end": v(-171.78, 211.81) * mm});
            skLineSegment(sketch, "E345", {"start": v(-175.07, 211.41) * mm, "end": v(-174.38, 211.81) * mm});
            skLineSegment(sketch, "E346", {"start": v(-180.27, 211.41) * mm, "end": v(-179.57, 211.81) * mm});
            skLineSegment(sketch, "E347", {"start": v(-173.68, 211.41) * mm, "end": v(-174.38, 211.81) * mm});
            skLineSegment(sketch, "E348", {"start": v(-178.88, 211.41) * mm, "end": v(-179.57, 211.81) * mm});
            skLineSegment(sketch, "E349", {"start": v(-179.41, 277.46) * mm, "end": v(-179.41, 288.94) * mm});
            skLineSegment(sketch, "E350", {"start": v(-175.19, 279.03) * mm, "end": v(-175.19, 288.94) * mm});
            skLineSegment(sketch, "E351", {"start": v(-177.3, 290.16) * mm, "end": v(-179.41, 288.94) * mm});
            skLineSegment(sketch, "E352", {"start": v(-177.3, 290.16) * mm, "end": v(-175.19, 288.94) * mm});
            skLineSegment(sketch, "E353", {"start": v(-177.3, 290.16) * mm, "end": v(-177.3, 280.63) * mm});
            skArc(sketch, "E354", {"start": v(-177.3, 280.63) * mm, "mid": v(-176.96, 279.49) * mm, "end": v(-176.05, 278.7) * mm});
            skLineSegment(sketch, "E355", {"start": v(-180.1, 257.11) * mm, "end": v(-179.41, 256.72) * mm});
            skLineSegment(sketch, "E356", {"start": v(-180.1, 257.11) * mm, "end": v(-179.41, 257.5) * mm});
            skLineSegment(sketch, "E357", {"start": v(-173.85, 258.93) * mm, "end": v(-174.54, 258.53) * mm});
            skLineSegment(sketch, "E358", {"start": v(-173.85, 258.93) * mm, "end": v(-174.54, 259.32) * mm});
            skLineSegment(sketch, "E359", {"start": v(-180.1, 257.11) * mm, "end": v(-173.85, 258.93) * mm});
            skLineSegment(sketch, "E360", {"start": v(-179.41, 256.72) * mm, "end": v(-174.54, 258.53) * mm});
            skLineSegment(sketch, "E361", {"start": v(-179.41, 257.5) * mm, "end": v(-174.54, 259.32) * mm});
            skLineSegment(sketch, "E362", {"start": v(-179.41, 256.72) * mm, "end": v(-179.41, 217.5) * mm});
            skLineSegment(sketch, "E363", {"start": v(-174.54, 258.53) * mm, "end": v(-174.54, 217.5) * mm});
            skLineSegment(sketch, "E364", {"start": v(-148.02, 412.03) * mm, "end": v(-148.02, 438.03) * mm});
            skLineSegment(sketch, "E365", {"start": v(187, 413.37) * mm, "end": v(187, 438.03) * mm});
            skLineSegment(sketch, "E366", {"start": v(-234.68, 434.85) * mm, "end": v(273.7, 434.85) * mm});
            skLineSegment(sketch, "E367", {"start": v(100.58, -60.7) * mm, "end": v(103.63, -60.7) * mm});
            skLineSegment(sketch, "E368", {"start": v(103.63, -60.7) * mm, "end": v(103.63, -75.11) * mm});
            skLineSegment(sketch, "E369", {"start": v(100.58, -60.7) * mm, "end": v(100.58, -75.11) * mm});
            skLineSegment(sketch, "E370", {"start": v(99, -79.75) * mm, "end": v(49, -79.75) * mm});
            skLineSegment(sketch, "E371", {"start": v(99, -76.7) * mm, "end": v(49, -76.7) * mm});
            skArc(sketch, "E372", {"start": v(48.23, -75.94) * mm, "mid": v(48.45, -76.48) * mm, "end": v(49, -76.7) * mm});
            skArc(sketch, "E373", {"start": v(45.18, -75.94) * mm, "mid": v(46.3, -78.63) * mm, "end": v(49, -79.75) * mm});
            skArc(sketch, "E374", {"start": v(99, -76.7) * mm, "mid": v(100.11, -76.23) * mm, "end": v(100.58, -75.11) * mm});
            skArc(sketch, "E375", {"start": v(99, -79.75) * mm, "mid": v(102.27, -78.39) * mm, "end": v(103.63, -75.11) * mm});
            skLineSegment(sketch, "E376", {"start": v(-10.55, -60.7) * mm, "end": v(-13.6, -60.7) * mm});
            skLineSegment(sketch, "E377", {"start": v(-13.6, -60.7) * mm, "end": v(-13.6, -75.11) * mm});
            skLineSegment(sketch, "E378", {"start": v(-10.55, -60.7) * mm, "end": v(-10.55, -75.11) * mm});
            skLineSegment(sketch, "E379", {"start": v(-8.96, -79.75) * mm, "end": v(40.73, -79.75) * mm});
            skLineSegment(sketch, "E380", {"start": v(-8.96, -76.7) * mm, "end": v(40.73, -76.7) * mm});
            skArc(sketch, "E381", {"start": v(40.73, -76.7) * mm, "mid": v(41.27, -76.48) * mm, "end": v(41.5, -75.94) * mm});
            skArc(sketch, "E382", {"start": v(40.73, -79.75) * mm, "mid": v(43.43, -78.63) * mm, "end": v(44.54, -75.94) * mm});
            skArc(sketch, "E383", {"start": v(-10.55, -75.11) * mm, "mid": v(-10.08, -76.23) * mm, "end": v(-8.96, -76.7) * mm});
            skArc(sketch, "E384", {"start": v(-13.6, -75.11) * mm, "mid": v(-12.24, -78.39) * mm, "end": v(-8.96, -79.75) * mm});
            skLineSegment(sketch, "E385", {"start": v(49.63, -162.09) * mm, "end": v(187.74, -162.09) * mm});
            skLineSegment(sketch, "E386", {"start": v(187.74, -86.69) * mm, "end": v(49.63, -86.69) * mm});
            skLineSegment(sketch, "E387", {"start": v(49.63, -87.49) * mm, "end": v(187.74, -87.49) * mm});
            skLineSegment(sketch, "E388", {"start": v(187.74, -162.89) * mm, "end": v(49.63, -162.89) * mm});
            skLineSegment(sketch, "E389", {"start": v(49.63, -162.89) * mm, "end": v(49.63, -86.69) * mm});
            skLineSegment(sketch, "E390", {"start": v(40.1, -162.09) * mm, "end": v(-105.22, -162.09) * mm});
            skLineSegment(sketch, "E391", {"start": v(-105.22, -86.69) * mm, "end": v(40.1, -86.69) * mm});
            skLineSegment(sketch, "E392", {"start": v(40.1, -87.49) * mm, "end": v(-105.22, -87.49) * mm});
            skLineSegment(sketch, "E393", {"start": v(-105.22, -162.89) * mm, "end": v(40.1, -162.89) * mm});
            skLineSegment(sketch, "E394", {"start": v(40.1, -162.89) * mm, "end": v(40.1, -86.69) * mm});
            skLineSegment(sketch, "E395", {"start": v(-105.22, -164.71) * mm, "end": v(-105.22, -120.76) * mm});
            skLineSegment(sketch, "E396", {"start": v(-105.22, -115.81) * mm, "end": v(-105.22, -84.15) * mm});
            skLineSegment(sketch, "E397", {"start": v(-105.22, -120.76) * mm, "end": v(-94.08, -118.26) * mm});
            skLineSegment(sketch, "E398", {"start": v(-117.4, -118.26) * mm, "end": v(-105.22, -115.81) * mm});
            skLineSegment(sketch, "E399", {"start": v(-117.4, -118.26) * mm, "end": v(-94.08, -118.26) * mm});
            skLineSegment(sketch, "E400", {"start": v(187.74, -164.71) * mm, "end": v(187.74, -120.76) * mm});
            skLineSegment(sketch, "E401", {"start": v(187.74, -115.81) * mm, "end": v(187.74, -84.15) * mm});
            skLineSegment(sketch, "E402", {"start": v(187.74, -120.76) * mm, "end": v(198.88, -118.26) * mm});
            skLineSegment(sketch, "E403", {"start": v(175.56, -118.26) * mm, "end": v(187.74, -115.81) * mm});
            skLineSegment(sketch, "E404", {"start": v(175.56, -118.26) * mm, "end": v(198.88, -118.26) * mm});
            skLineSegment(sketch, "E405", {"start": v(-19.05, -169.3) * mm, "end": v(108.77, -169.3) * mm});
            skLineSegment(sketch, "E406", {"start": v(-18.84, -167.77) * mm, "end": v(108.57, -167.77) * mm});
            skLineSegment(sketch, "E407", {"start": v(108.57, -167.77) * mm, "end": v(119.2, -164.92) * mm});
            skLineSegment(sketch, "E408", {"start": v(108.77, -169.3) * mm, "end": v(119.6, -166.4) * mm});
            skLineSegment(sketch, "E409", {"start": v(-18.84, -167.77) * mm, "end": v(-29.47, -164.92) * mm});
            skLineSegment(sketch, "E410", {"start": v(-19.05, -169.3) * mm, "end": v(-29.87, -166.4) * mm});
            skLineSegment(sketch, "E411", {"start": v(-18.84, -81.48) * mm, "end": v(108.56, -81.48) * mm});
            skLineSegment(sketch, "E412", {"start": v(-18.64, -83) * mm, "end": v(108.36, -83) * mm});
            skLineSegment(sketch, "E413", {"start": v(108.36, -83) * mm, "end": v(119.16, -83) * mm});
            skLineSegment(sketch, "E414", {"start": v(108.16, -81.48) * mm, "end": v(119.16, -81.48) * mm});
            skLineSegment(sketch, "E415", {"start": v(-18.64, -83) * mm, "end": v(-29.43, -83) * mm});
            skLineSegment(sketch, "E416", {"start": v(-18.43, -81.48) * mm, "end": v(-29.43, -81.48) * mm});
            skLineSegment(sketch, "E417", {"start": v(187.74, -130.36) * mm, "end": v(49.63, -130.36) * mm});
            skLineSegment(sketch, "E418", {"start": v(40.1, -130.36) * mm, "end": v(-105.22, -130.36) * mm});
            skLineSegment(sketch, "E419", {"start": v(187.74, -131.16) * mm, "end": v(49.63, -131.16) * mm});
            skLineSegment(sketch, "E420", {"start": v(40.1, -131.16) * mm, "end": v(-105.22, -131.16) * mm});
            skLineSegment(sketch, "E421", {"start": v(50.63, -132.01) * mm, "end": v(152.23, -132.01) * mm});
            skLineSegment(sketch, "E422", {"start": v(50.63, -134.28) * mm, "end": v(152.23, -134.28) * mm});
            skLineSegment(sketch, "E423", {"start": v(50.63, -134.85) * mm, "end": v(152.23, -134.85) * mm});
            skLineSegment(sketch, "E424", {"start": v(50.63, -132.01) * mm, "end": v(50.63, -134.85) * mm});
            skLineSegment(sketch, "E425", {"start": v(152.23, -132.01) * mm, "end": v(152.23, -134.85) * mm});
            skLineSegment(sketch, "E426", {"start": v(-62.42, -132.01) * mm, "end": v(39.18, -132.01) * mm});
            skLineSegment(sketch, "E427", {"start": v(-62.42, -134.28) * mm, "end": v(39.18, -134.28) * mm});
            skLineSegment(sketch, "E428", {"start": v(-62.42, -134.85) * mm, "end": v(39.18, -134.85) * mm});
            skLineSegment(sketch, "E429", {"start": v(-62.42, -132.01) * mm, "end": v(-62.42, -134.85) * mm});
            skLineSegment(sketch, "E430", {"start": v(39.18, -132.01) * mm, "end": v(39.18, -134.85) * mm});
            skLineSegment(sketch, "E431", {"start": v(22.26, -136.63) * mm, "end": v(22.26, -135.36) * mm});
            skLineSegment(sketch, "E432", {"start": v(9.05, -136.63) * mm, "end": v(9.05, -135.36) * mm});
            skLineSegment(sketch, "E433", {"start": v(20.85, -141.05) * mm, "end": v(20.85, -136.63) * mm});
            skLineSegment(sketch, "E434", {"start": v(10.46, -141.05) * mm, "end": v(10.46, -136.63) * mm});
            skLineSegment(sketch, "E435", {"start": v(18.1, -93.54) * mm, "end": v(18.1, -92.52) * mm});
            skLineSegment(sketch, "E436", {"start": v(18.1, -91.73) * mm, "end": v(18.1, -90.7) * mm});
            skLineSegment(sketch, "E437", {"start": v(18.1, -89.92) * mm, "end": v(18.1, -88.9) * mm});
            skLineSegment(sketch, "E438", {"start": v(18.1, -88.1) * mm, "end": v(18.1, -87.08) * mm});
            skLineSegment(sketch, "E439", {"start": v(18.1, -86.3) * mm, "end": v(18.1, -85.27) * mm});
            skLineSegment(sketch, "E440", {"start": v(18.1, -84.48) * mm, "end": v(18.1, -83.46) * mm});
            skLineSegment(sketch, "E441", {"start": v(18.1, -82.66) * mm, "end": v(18.1, -81.64) * mm});
            skLineSegment(sketch, "E442", {"start": v(18.1, -80.85) * mm, "end": v(18.1, -79.83) * mm});
            skLineSegment(sketch, "E443", {"start": v(18.1, -79.04) * mm, "end": v(18.1, -78.01) * mm});
            skLineSegment(sketch, "E444", {"start": v(18.1, -77.22) * mm, "end": v(18.1, -76.2) * mm});
            skLineSegment(sketch, "E445", {"start": v(18.1, -75.4) * mm, "end": v(18.1, -74.39) * mm});
            skLineSegment(sketch, "E446", {"start": v(13.22, -95.36) * mm, "end": v(13.22, -94.34) * mm});
            skLineSegment(sketch, "E447", {"start": v(13.22, -93.54) * mm, "end": v(13.22, -92.52) * mm});
            skLineSegment(sketch, "E448", {"start": v(13.22, -91.73) * mm, "end": v(13.22, -90.7) * mm});
            skLineSegment(sketch, "E449", {"start": v(13.22, -89.92) * mm, "end": v(13.22, -88.9) * mm});
            skLineSegment(sketch, "E450", {"start": v(13.22, -88.1) * mm, "end": v(13.22, -87.08) * mm});
            skLineSegment(sketch, "E451", {"start": v(13.22, -86.3) * mm, "end": v(13.22, -85.27) * mm});
            skLineSegment(sketch, "E452", {"start": v(13.22, -84.48) * mm, "end": v(13.22, -83.46) * mm});
            skLineSegment(sketch, "E453", {"start": v(13.22, -82.66) * mm, "end": v(13.22, -81.64) * mm});
            skLineSegment(sketch, "E454", {"start": v(13.22, -80.85) * mm, "end": v(13.22, -79.83) * mm});
            skLineSegment(sketch, "E455", {"start": v(13.22, -79.04) * mm, "end": v(13.22, -78.01) * mm});
            skLineSegment(sketch, "E456", {"start": v(13.22, -77.22) * mm, "end": v(13.22, -76.2) * mm});
            skLineSegment(sketch, "E457", {"start": v(12.53, -93.94) * mm, "end": v(13.22, -94.34) * mm});
            skLineSegment(sketch, "E458", {"start": v(12.53, -93.94) * mm, "end": v(13.22, -93.54) * mm});
            skLineSegment(sketch, "E459", {"start": v(12.53, -92.13) * mm, "end": v(13.22, -92.52) * mm});
            skLineSegment(sketch, "E460", {"start": v(12.53, -92.13) * mm, "end": v(13.22, -91.73) * mm});
            skLineSegment(sketch, "E461", {"start": v(18.78, -92.13) * mm, "end": v(18.1, -92.52) * mm});
            skLineSegment(sketch, "E462", {"start": v(18.78, -92.13) * mm, "end": v(18.1, -91.73) * mm});
            skLineSegment(sketch, "E463", {"start": v(18.78, -90.31) * mm, "end": v(18.1, -90.7) * mm});
            skLineSegment(sketch, "E464", {"start": v(18.78, -90.31) * mm, "end": v(18.1, -89.92) * mm});
            skLineSegment(sketch, "E465", {"start": v(12.53, -93.94) * mm, "end": v(18.78, -92.13) * mm});
            skLineSegment(sketch, "E466", {"start": v(12.53, -92.13) * mm, "end": v(18.78, -90.31) * mm});
            skLineSegment(sketch, "E467", {"start": v(13.22, -94.34) * mm, "end": v(18.1, -92.52) * mm});
            skLineSegment(sketch, "E468", {"start": v(13.22, -93.54) * mm, "end": v(18.1, -91.73) * mm});
            skLineSegment(sketch, "E469", {"start": v(13.22, -92.52) * mm, "end": v(18.1, -90.7) * mm});
            skLineSegment(sketch, "E470", {"start": v(13.22, -91.73) * mm, "end": v(18.1, -89.92) * mm});
            skLineSegment(sketch, "E471", {"start": v(12.53, -90.31) * mm, "end": v(13.22, -90.7) * mm});
            skLineSegment(sketch, "E472", {"start": v(12.53, -90.31) * mm, "end": v(13.22, -89.92) * mm});
            skLineSegment(sketch, "E473", {"start": v(12.53, -88.5) * mm, "end": v(13.22, -88.9) * mm});
            skLineSegment(sketch, "E474", {"start": v(12.53, -88.5) * mm, "end": v(13.22, -88.1) * mm});
            skLineSegment(sketch, "E475", {"start": v(18.78, -88.5) * mm, "end": v(18.1, -88.9) * mm});
            skLineSegment(sketch, "E476", {"start": v(18.78, -88.5) * mm, "end": v(18.1, -88.1) * mm});
            skLineSegment(sketch, "E477", {"start": v(18.78, -86.69) * mm, "end": v(18.1, -87.08) * mm});
            skLineSegment(sketch, "E478", {"start": v(18.78, -86.69) * mm, "end": v(18.1, -86.3) * mm});
            skLineSegment(sketch, "E479", {"start": v(12.53, -90.31) * mm, "end": v(18.78, -88.5) * mm});
            skLineSegment(sketch, "E480", {"start": v(12.53, -88.5) * mm, "end": v(18.78, -86.69) * mm});
            skLineSegment(sketch, "E481", {"start": v(13.22, -90.7) * mm, "end": v(18.1, -88.9) * mm});
            skLineSegment(sketch, "E482", {"start": v(13.22, -89.92) * mm, "end": v(18.1, -88.1) * mm});
            skLineSegment(sketch, "E483", {"start": v(13.22, -88.9) * mm, "end": v(18.1, -87.08) * mm});
            skLineSegment(sketch, "E484", {"start": v(13.22, -88.1) * mm, "end": v(18.1, -86.3) * mm});
            skLineSegment(sketch, "E485", {"start": v(12.53, -86.69) * mm, "end": v(13.22, -87.08) * mm});
            skLineSegment(sketch, "E486", {"start": v(12.53, -86.69) * mm, "end": v(13.22, -86.3) * mm});
            skLineSegment(sketch, "E487", {"start": v(18.78, -84.87) * mm, "end": v(18.1, -85.27) * mm});
            skLineSegment(sketch, "E488", {"start": v(18.78, -84.87) * mm, "end": v(18.1, -84.48) * mm});
            skLineSegment(sketch, "E489", {"start": v(12.53, -86.69) * mm, "end": v(18.78, -84.87) * mm});
            skLineSegment(sketch, "E490", {"start": v(13.22, -87.08) * mm, "end": v(18.1, -85.27) * mm});
            skLineSegment(sketch, "E491", {"start": v(13.22, -86.3) * mm, "end": v(18.1, -84.48) * mm});
            skLineSegment(sketch, "E492", {"start": v(12.53, -84.87) * mm, "end": v(13.22, -85.27) * mm});
            skLineSegment(sketch, "E493", {"start": v(12.53, -84.87) * mm, "end": v(13.22, -84.48) * mm});
            skLineSegment(sketch, "E494", {"start": v(12.53, -83.06) * mm, "end": v(13.22, -83.46) * mm});
            skLineSegment(sketch, "E495", {"start": v(12.53, -83.06) * mm, "end": v(13.22, -82.66) * mm});
            skLineSegment(sketch, "E496", {"start": v(18.78, -83.06) * mm, "end": v(18.1, -83.46) * mm});
            skLineSegment(sketch, "E497", {"start": v(18.78, -83.06) * mm, "end": v(18.1, -82.66) * mm});
            skLineSegment(sketch, "E498", {"start": v(18.78, -81.25) * mm, "end": v(18.1, -81.64) * mm});
            skLineSegment(sketch, "E499", {"start": v(18.78, -81.25) * mm, "end": v(18.1, -80.85) * mm});
            skLineSegment(sketch, "E500", {"start": v(12.53, -84.87) * mm, "end": v(18.78, -83.06) * mm});
            skLineSegment(sketch, "E501", {"start": v(12.53, -83.06) * mm, "end": v(18.78, -81.25) * mm});
            skLineSegment(sketch, "E502", {"start": v(13.22, -85.27) * mm, "end": v(18.1, -83.46) * mm});
            skLineSegment(sketch, "E503", {"start": v(13.22, -84.48) * mm, "end": v(18.1, -82.66) * mm});
            skLineSegment(sketch, "E504", {"start": v(13.22, -83.46) * mm, "end": v(18.1, -81.64) * mm});
            skLineSegment(sketch, "E505", {"start": v(13.22, -82.66) * mm, "end": v(18.1, -80.85) * mm});
            skLineSegment(sketch, "E506", {"start": v(12.53, -81.25) * mm, "end": v(13.22, -81.64) * mm});
            skLineSegment(sketch, "E507", {"start": v(12.53, -81.25) * mm, "end": v(13.22, -80.85) * mm});
            skLineSegment(sketch, "E508", {"start": v(12.53, -79.43) * mm, "end": v(13.22, -79.83) * mm});
            skLineSegment(sketch, "E509", {"start": v(12.53, -79.43) * mm, "end": v(13.22, -79.04) * mm});
            skLineSegment(sketch, "E510", {"start": v(18.78, -79.43) * mm, "end": v(18.1, -79.83) * mm});
            skLineSegment(sketch, "E511", {"start": v(18.78, -79.43) * mm, "end": v(18.1, -79.04) * mm});
            skLineSegment(sketch, "E512", {"start": v(18.78, -77.62) * mm, "end": v(18.1, -78.01) * mm});
            skLineSegment(sketch, "E513", {"start": v(18.78, -77.62) * mm, "end": v(18.1, -77.22) * mm});
            skLineSegment(sketch, "E514", {"start": v(12.53, -81.25) * mm, "end": v(18.78, -79.43) * mm});
            skLineSegment(sketch, "E515", {"start": v(12.53, -79.43) * mm, "end": v(18.78, -77.62) * mm});
            skLineSegment(sketch, "E516", {"start": v(13.22, -81.64) * mm, "end": v(18.1, -79.83) * mm});
            skLineSegment(sketch, "E517", {"start": v(13.22, -80.85) * mm, "end": v(18.1, -79.04) * mm});
            skLineSegment(sketch, "E518", {"start": v(13.22, -79.83) * mm, "end": v(18.1, -78.01) * mm});
            skLineSegment(sketch, "E519", {"start": v(13.22, -79.04) * mm, "end": v(18.1, -77.22) * mm});
            skLineSegment(sketch, "E520", {"start": v(12.53, -77.62) * mm, "end": v(13.22, -78.01) * mm});
            skLineSegment(sketch, "E521", {"start": v(12.53, -77.62) * mm, "end": v(13.22, -77.22) * mm});
            skLineSegment(sketch, "E522", {"start": v(12.53, -75.8) * mm, "end": v(13.22, -76.2) * mm});
            skLineSegment(sketch, "E523", {"start": v(12.53, -75.8) * mm, "end": v(13.22, -75.4) * mm});
            skLineSegment(sketch, "E524", {"start": v(18.78, -75.8) * mm, "end": v(18.1, -76.2) * mm});
            skLineSegment(sketch, "E525", {"start": v(18.78, -75.8) * mm, "end": v(18.1, -75.4) * mm});
            skLineSegment(sketch, "E526", {"start": v(18.78, -74) * mm, "end": v(18.1, -74.39) * mm});
            skLineSegment(sketch, "E527", {"start": v(18.78, -74) * mm, "end": v(18.1, -73.6) * mm});
            skLineSegment(sketch, "E528", {"start": v(12.53, -77.62) * mm, "end": v(18.78, -75.8) * mm});
            skLineSegment(sketch, "E529", {"start": v(12.53, -75.8) * mm, "end": v(18.78, -74) * mm});
            skLineSegment(sketch, "E530", {"start": v(13.22, -78.01) * mm, "end": v(18.1, -76.2) * mm});
            skLineSegment(sketch, "E531", {"start": v(13.22, -77.22) * mm, "end": v(18.1, -75.4) * mm});
            skLineSegment(sketch, "E532", {"start": v(13.22, -76.2) * mm, "end": v(18.1, -74.39) * mm});
            skLineSegment(sketch, "E533", {"start": v(13.22, -75.4) * mm, "end": v(18.1, -73.6) * mm});
            skLineSegment(sketch, "E534", {"start": v(9.05, -135.36) * mm, "end": v(22.26, -135.36) * mm});
            skLineSegment(sketch, "E535", {"start": v(9.05, -136.63) * mm, "end": v(22.26, -136.63) * mm});
            skLineSegment(sketch, "E536", {"start": v(11.15, -141.45) * mm, "end": v(20.15, -141.45) * mm});
            skLineSegment(sketch, "E537", {"start": v(13.06, -141.05) * mm, "end": v(13.06, -136.63) * mm});
            skLineSegment(sketch, "E538", {"start": v(18.25, -141.05) * mm, "end": v(18.25, -136.63) * mm});
            skLineSegment(sketch, "E539", {"start": v(11.15, -141.45) * mm, "end": v(10.46, -141.05) * mm});
            skLineSegment(sketch, "E540", {"start": v(20.15, -141.45) * mm, "end": v(20.85, -141.05) * mm});
            skLineSegment(sketch, "E541", {"start": v(17.55, -141.45) * mm, "end": v(18.25, -141.05) * mm});
            skLineSegment(sketch, "E542", {"start": v(12.36, -141.45) * mm, "end": v(13.06, -141.05) * mm});
            skLineSegment(sketch, "E543", {"start": v(18.95, -141.45) * mm, "end": v(18.25, -141.05) * mm});
            skLineSegment(sketch, "E544", {"start": v(13.75, -141.45) * mm, "end": v(13.06, -141.05) * mm});
            skLineSegment(sketch, "E545", {"start": v(13.22, -75.4) * mm, "end": v(13.22, -63.93) * mm});
            skLineSegment(sketch, "E546", {"start": v(17.44, -73.84) * mm, "end": v(17.44, -63.93) * mm});
            skLineSegment(sketch, "E547", {"start": v(15.33, -62.7) * mm, "end": v(13.22, -63.93) * mm});
            skLineSegment(sketch, "E548", {"start": v(15.33, -62.7) * mm, "end": v(17.44, -63.93) * mm});
            skLineSegment(sketch, "E549", {"start": v(15.33, -62.7) * mm, "end": v(15.33, -72.23) * mm});
            skArc(sketch, "E550", {"start": v(15.33, -72.23) * mm, "mid": v(15.67, -73.38) * mm, "end": v(16.57, -74.16) * mm});
            skLineSegment(sketch, "E551", {"start": v(12.53, -95.75) * mm, "end": v(13.22, -96.15) * mm});
            skLineSegment(sketch, "E552", {"start": v(12.53, -95.75) * mm, "end": v(13.22, -95.36) * mm});
            skLineSegment(sketch, "E553", {"start": v(18.78, -93.94) * mm, "end": v(18.1, -94.34) * mm});
            skLineSegment(sketch, "E554", {"start": v(18.78, -93.94) * mm, "end": v(18.1, -93.54) * mm});
            skLineSegment(sketch, "E555", {"start": v(12.53, -95.75) * mm, "end": v(18.78, -93.94) * mm});
            skLineSegment(sketch, "E556", {"start": v(13.22, -96.15) * mm, "end": v(18.1, -94.34) * mm});
            skLineSegment(sketch, "E557", {"start": v(13.22, -95.36) * mm, "end": v(18.1, -93.54) * mm});
            skLineSegment(sketch, "E558", {"start": v(13.22, -96.15) * mm, "end": v(13.22, -135.36) * mm});
            skLineSegment(sketch, "E559", {"start": v(18.1, -94.34) * mm, "end": v(18.1, -135.36) * mm});
            skLineSegment(sketch, "E560", {"start": v(-29.43, -83) * mm, "end": v(-29.43, -81.48) * mm});
            skLineSegment(sketch, "E561", {"start": v(119.16, -83) * mm, "end": v(119.16, -81.48) * mm});
            skLineSegment(sketch, "E562", {"start": v(119.2, -164.92) * mm, "end": v(119.6, -166.4) * mm});
            skLineSegment(sketch, "E563", {"start": v(-29.87, -166.4) * mm, "end": v(-29.47, -164.92) * mm});
            skLineSegment(sketch, "E564", {"start": v(-27.1, -165.55) * mm, "end": v(2.6, -165.55) * mm});
            skLineSegment(sketch, "E565", {"start": v(-29.16, -164.03) * mm, "end": v(2.6, -164.03) * mm});
            skLineSegment(sketch, "E566", {"start": v(-29.16, -164.03) * mm, "end": v(-29.16, -165) * mm});
            skLineSegment(sketch, "E567", {"start": v(2.6, -164.03) * mm, "end": v(2.6, -165.55) * mm});
            skLineSegment(sketch, "E568", {"start": v(87.33, -165.55) * mm, "end": v(116.83, -165.55) * mm});
            skLineSegment(sketch, "E569", {"start": v(87.33, -164.03) * mm, "end": v(119.08, -164.03) * mm});
            skLineSegment(sketch, "E570", {"start": v(87.33, -164.03) * mm, "end": v(87.33, -165.55) * mm});
            skLineSegment(sketch, "E571", {"start": v(119.08, -164.03) * mm, "end": v(119.08, -164.95) * mm});
            skLineSegment(sketch, "E572", {"start": v(-4.94, -85.56) * mm, "end": v(34.87, -85.56) * mm});
            skLineSegment(sketch, "E573", {"start": v(-4.94, -84.04) * mm, "end": v(34.87, -84.04) * mm});
            skLineSegment(sketch, "E574", {"start": v(-4.94, -84.04) * mm, "end": v(-4.94, -85.56) * mm});
            skLineSegment(sketch, "E575", {"start": v(34.87, -84.04) * mm, "end": v(34.87, -85.56) * mm});
            skLineSegment(sketch, "E576", {"start": v(55.88, -85.56) * mm, "end": v(94.6, -85.56) * mm});
            skLineSegment(sketch, "E577", {"start": v(55.88, -84.04) * mm, "end": v(94.6, -84.04) * mm});
            skLineSegment(sketch, "E578", {"start": v(55.88, -84.04) * mm, "end": v(55.88, -85.56) * mm});
            skLineSegment(sketch, "E579", {"start": v(94.6, -84.04) * mm, "end": v(94.6, -85.56) * mm});
            skLineSegment(sketch, "E580", {"start": v(-5.7, -170.24) * mm, "end": v(-17.48, -170.24) * mm});
            skLineSegment(sketch, "E581", {"start": v(-8.9, -166.58) * mm, "end": v(-9.58, -166.19) * mm});
            skLineSegment(sketch, "E582", {"start": v(-8.9, -166.58) * mm, "end": v(-9.58, -166.97) * mm});
            skLineSegment(sketch, "E583", {"start": v(-14.28, -166.58) * mm, "end": v(-13.6, -166.97) * mm});
            skLineSegment(sketch, "E584", {"start": v(-14.28, -166.58) * mm, "end": v(-13.6, -166.19) * mm});
            skLineSegment(sketch, "E585", {"start": v(-8.9, -163.02) * mm, "end": v(-9.58, -162.63) * mm});
            skLineSegment(sketch, "E586", {"start": v(-8.9, -163.02) * mm, "end": v(-9.58, -163.42) * mm});
            skLineSegment(sketch, "E587", {"start": v(-8.9, -161.24) * mm, "end": v(-9.58, -160.85) * mm});
            skLineSegment(sketch, "E588", {"start": v(-8.9, -161.24) * mm, "end": v(-9.58, -161.64) * mm});
            skLineSegment(sketch, "E589", {"start": v(-14.28, -163.02) * mm, "end": v(-8.9, -161.24) * mm});
            skLineSegment(sketch, "E590", {"start": v(-9.58, -160.85) * mm, "end": v(-13.6, -162.63) * mm});
            skLineSegment(sketch, "E591", {"start": v(-13.6, -163.42) * mm, "end": v(-9.58, -161.64) * mm});
            skLineSegment(sketch, "E592", {"start": v(-14.28, -163.02) * mm, "end": v(-13.6, -163.42) * mm});
            skLineSegment(sketch, "E593", {"start": v(-14.28, -163.02) * mm, "end": v(-13.6, -162.63) * mm});
            skLineSegment(sketch, "E594", {"start": v(-8.9, -159.46) * mm, "end": v(-9.58, -159.07) * mm});
            skLineSegment(sketch, "E595", {"start": v(-8.9, -159.46) * mm, "end": v(-9.58, -159.86) * mm});
            skLineSegment(sketch, "E596", {"start": v(-14.28, -161.24) * mm, "end": v(-8.9, -159.46) * mm});
            skLineSegment(sketch, "E597", {"start": v(-9.58, -159.07) * mm, "end": v(-13.6, -160.85) * mm});
            skLineSegment(sketch, "E598", {"start": v(-13.6, -161.64) * mm, "end": v(-9.58, -159.86) * mm});
            skLineSegment(sketch, "E599", {"start": v(-14.28, -161.24) * mm, "end": v(-13.6, -161.64) * mm});
            skLineSegment(sketch, "E600", {"start": v(-14.28, -161.24) * mm, "end": v(-13.6, -160.85) * mm});
            skLineSegment(sketch, "E601", {"start": v(-8.9, -157.68) * mm, "end": v(-9.58, -157.29) * mm});
            skLineSegment(sketch, "E602", {"start": v(-8.9, -157.68) * mm, "end": v(-9.58, -158.08) * mm});
            skLineSegment(sketch, "E603", {"start": v(-14.28, -159.46) * mm, "end": v(-8.9, -157.68) * mm});
            skLineSegment(sketch, "E604", {"start": v(-9.58, -157.29) * mm, "end": v(-13.6, -159.07) * mm});
            skLineSegment(sketch, "E605", {"start": v(-13.6, -159.86) * mm, "end": v(-9.58, -158.08) * mm});
            skLineSegment(sketch, "E606", {"start": v(-14.28, -159.46) * mm, "end": v(-13.6, -159.86) * mm});
            skLineSegment(sketch, "E607", {"start": v(-14.28, -159.46) * mm, "end": v(-13.6, -159.07) * mm});
            skLineSegment(sketch, "E608", {"start": v(-14.28, -157.68) * mm, "end": v(-11.6, -157.19) * mm});
            skLineSegment(sketch, "E609", {"start": v(-11.6, -157.19) * mm, "end": v(-13.6, -157.29) * mm});
            skLineSegment(sketch, "E610", {"start": v(-13.6, -158.08) * mm, "end": v(-11.6, -157.19) * mm});
            skLineSegment(sketch, "E611", {"start": v(-14.28, -157.68) * mm, "end": v(-13.6, -158.08) * mm});
            skLineSegment(sketch, "E612", {"start": v(-14.28, -157.68) * mm, "end": v(-13.6, -157.29) * mm});
            skLineSegment(sketch, "E613", {"start": v(-13.6, -158.08) * mm, "end": v(-13.6, -159.07) * mm});
            skLineSegment(sketch, "E614", {"start": v(-9.58, -158.08) * mm, "end": v(-9.58, -159.07) * mm});
            skLineSegment(sketch, "E615", {"start": v(-9.58, -159.86) * mm, "end": v(-9.58, -160.85) * mm});
            skLineSegment(sketch, "E616", {"start": v(-9.58, -161.64) * mm, "end": v(-9.58, -162.63) * mm});
            skLineSegment(sketch, "E617", {"start": v(-9.58, -166.97) * mm, "end": v(-9.58, -167.97) * mm});
            skLineSegment(sketch, "E618", {"start": v(-13.6, -161.64) * mm, "end": v(-13.6, -162.63) * mm});
            skLineSegment(sketch, "E619", {"start": v(-13.6, -159.86) * mm, "end": v(-13.6, -160.85) * mm});
            skLineSegment(sketch, "E620", {"start": v(-14.28, -170.14) * mm, "end": v(-13.6, -169.74) * mm});
            skLineSegment(sketch, "E621", {"start": v(-14.28, -170.14) * mm, "end": v(-14.11, -170.24) * mm});
            skLineSegment(sketch, "E622", {"start": v(-5.7, -171.12) * mm, "end": v(-17.48, -171.12) * mm});
            skLineSegment(sketch, "E623", {"start": v(-17.48, -170.24) * mm, "end": v(-17.48, -171.12) * mm});
            skLineSegment(sketch, "E624", {"start": v(-5.7, -170.24) * mm, "end": v(-5.7, -171.12) * mm});
            skLineSegment(sketch, "E625", {"start": v(-7.92, -174.54) * mm, "end": v(-15.33, -174.54) * mm});
            skLineSegment(sketch, "E626", {"start": v(-6.75, -171.12) * mm, "end": v(-6.75, -173.47) * mm});
            skLineSegment(sketch, "E627", {"start": v(-16.43, -171.12) * mm, "end": v(-16.43, -173.47) * mm});
            skLineSegment(sketch, "E628", {"start": v(-14.16, -173.47) * mm, "end": v(-14.16, -171.12) * mm});
            skLineSegment(sketch, "E629", {"start": v(-9.03, -173.47) * mm, "end": v(-9.03, -171.12) * mm});
            skArc(sketch, "E630", {"start": v(-14.16, -173.47) * mm, "mid": v(-11.6, -174.54) * mm, "end": v(-9.03, -173.47) * mm});
            skArc(sketch, "E631", {"start": v(-9.03, -173.47) * mm, "mid": v(-7.89, -174.54) * mm, "end": v(-6.75, -173.47) * mm});
            skArc(sketch, "E632", {"start": v(-16.43, -173.47) * mm, "mid": v(-15.3, -174.54) * mm, "end": v(-14.16, -173.47) * mm});
            skLineSegment(sketch, "E633", {"start": v(-13.6, -157.29) * mm, "end": v(-13.6, -152.35) * mm});
            skLineSegment(sketch, "E634", {"start": v(-9.58, -157.29) * mm, "end": v(-9.58, -152.35) * mm});
            skLineSegment(sketch, "E635", {"start": v(-11.6, -151.19) * mm, "end": v(-13.6, -152.35) * mm});
            skLineSegment(sketch, "E636", {"start": v(-11.6, -151.19) * mm, "end": v(-9.58, -152.35) * mm});
            skLineSegment(sketch, "E637", {"start": v(-11.6, -151.19) * mm, "end": v(-11.6, -153.73) * mm});
            skArc(sketch, "E638", {"start": v(-11.6, -153.73) * mm, "mid": v(-11, -155.15) * mm, "end": v(-9.58, -155.74) * mm});
            skLineSegment(sketch, "E639", {"start": v(107.15, -170.24) * mm, "end": v(95.36, -170.24) * mm});
            skLineSegment(sketch, "E640", {"start": v(103.94, -166.58) * mm, "end": v(103.26, -166.19) * mm});
            skLineSegment(sketch, "E641", {"start": v(103.94, -166.58) * mm, "end": v(103.26, -166.97) * mm});
            skLineSegment(sketch, "E642", {"start": v(98.56, -166.58) * mm, "end": v(99.24, -166.97) * mm});
            skLineSegment(sketch, "E643", {"start": v(98.56, -166.58) * mm, "end": v(99.24, -166.19) * mm});
            skLineSegment(sketch, "E644", {"start": v(103.94, -163.02) * mm, "end": v(103.26, -162.63) * mm});
            skLineSegment(sketch, "E645", {"start": v(103.94, -163.02) * mm, "end": v(103.26, -163.42) * mm});
            skLineSegment(sketch, "E646", {"start": v(103.94, -161.24) * mm, "end": v(103.26, -160.85) * mm});
            skLineSegment(sketch, "E647", {"start": v(103.94, -161.24) * mm, "end": v(103.26, -161.64) * mm});
            skLineSegment(sketch, "E648", {"start": v(98.56, -163.02) * mm, "end": v(103.94, -161.24) * mm});
            skLineSegment(sketch, "E649", {"start": v(103.26, -160.85) * mm, "end": v(99.24, -162.63) * mm});
            skLineSegment(sketch, "E650", {"start": v(99.24, -163.42) * mm, "end": v(103.26, -161.64) * mm});
            skLineSegment(sketch, "E651", {"start": v(98.56, -163.02) * mm, "end": v(99.24, -163.42) * mm});
            skLineSegment(sketch, "E652", {"start": v(98.56, -163.02) * mm, "end": v(99.24, -162.63) * mm});
            skLineSegment(sketch, "E653", {"start": v(103.94, -159.46) * mm, "end": v(103.26, -159.07) * mm});
            skLineSegment(sketch, "E654", {"start": v(103.94, -159.46) * mm, "end": v(103.26, -159.86) * mm});
            skLineSegment(sketch, "E655", {"start": v(98.56, -161.24) * mm, "end": v(103.94, -159.46) * mm});
            skLineSegment(sketch, "E656", {"start": v(103.26, -159.07) * mm, "end": v(99.24, -160.85) * mm});
            skLineSegment(sketch, "E657", {"start": v(99.24, -161.64) * mm, "end": v(103.26, -159.86) * mm});
            skLineSegment(sketch, "E658", {"start": v(98.56, -161.24) * mm, "end": v(99.24, -161.64) * mm});
            skLineSegment(sketch, "E659", {"start": v(98.56, -161.24) * mm, "end": v(99.24, -160.85) * mm});
            skLineSegment(sketch, "E660", {"start": v(103.94, -157.68) * mm, "end": v(103.26, -157.29) * mm});
            skLineSegment(sketch, "E661", {"start": v(103.94, -157.68) * mm, "end": v(103.26, -158.08) * mm});
            skLineSegment(sketch, "E662", {"start": v(98.56, -159.46) * mm, "end": v(103.94, -157.68) * mm});
            skLineSegment(sketch, "E663", {"start": v(103.26, -157.29) * mm, "end": v(99.24, -159.07) * mm});
            skLineSegment(sketch, "E664", {"start": v(99.24, -159.86) * mm, "end": v(103.26, -158.08) * mm});
            skLineSegment(sketch, "E665", {"start": v(98.56, -159.46) * mm, "end": v(99.24, -159.86) * mm});
            skLineSegment(sketch, "E666", {"start": v(98.56, -159.46) * mm, "end": v(99.24, -159.07) * mm});
            skLineSegment(sketch, "E667", {"start": v(98.56, -157.68) * mm, "end": v(101.25, -157.19) * mm});
            skLineSegment(sketch, "E668", {"start": v(101.25, -157.19) * mm, "end": v(99.24, -157.29) * mm});
            skLineSegment(sketch, "E669", {"start": v(99.24, -158.08) * mm, "end": v(101.25, -157.19) * mm});
            skLineSegment(sketch, "E670", {"start": v(98.56, -157.68) * mm, "end": v(99.24, -158.08) * mm});
            skLineSegment(sketch, "E671", {"start": v(98.56, -157.68) * mm, "end": v(99.24, -157.29) * mm});
            skLineSegment(sketch, "E672", {"start": v(99.24, -158.08) * mm, "end": v(99.24, -159.07) * mm});
            skLineSegment(sketch, "E673", {"start": v(103.26, -158.08) * mm, "end": v(103.26, -159.07) * mm});
            skLineSegment(sketch, "E674", {"start": v(103.26, -159.86) * mm, "end": v(103.26, -160.85) * mm});
            skLineSegment(sketch, "E675", {"start": v(103.26, -161.64) * mm, "end": v(103.26, -162.63) * mm});
            skLineSegment(sketch, "E676", {"start": v(99.24, -161.64) * mm, "end": v(99.24, -162.63) * mm});
            skLineSegment(sketch, "E677", {"start": v(99.24, -159.86) * mm, "end": v(99.24, -160.85) * mm});
            skLineSegment(sketch, "E678", {"start": v(98.56, -170.14) * mm, "end": v(99.24, -169.74) * mm});
            skLineSegment(sketch, "E679", {"start": v(98.56, -170.14) * mm, "end": v(98.73, -170.24) * mm});
            skLineSegment(sketch, "E680", {"start": v(107.15, -171.12) * mm, "end": v(95.36, -171.12) * mm});
            skLineSegment(sketch, "E681", {"start": v(95.36, -170.24) * mm, "end": v(95.36, -171.12) * mm});
            skLineSegment(sketch, "E682", {"start": v(107.15, -170.24) * mm, "end": v(107.15, -171.12) * mm});
            skLineSegment(sketch, "E683", {"start": v(104.92, -174.54) * mm, "end": v(97.51, -174.54) * mm});
            skLineSegment(sketch, "E684", {"start": v(106.1, -171.12) * mm, "end": v(106.1, -173.47) * mm});
            skLineSegment(sketch, "E685", {"start": v(96.41, -171.12) * mm, "end": v(96.41, -173.47) * mm});
            skLineSegment(sketch, "E686", {"start": v(98.69, -173.47) * mm, "end": v(98.69, -171.12) * mm});
            skLineSegment(sketch, "E687", {"start": v(103.82, -173.47) * mm, "end": v(103.82, -171.12) * mm});
            skArc(sketch, "E688", {"start": v(98.69, -173.47) * mm, "mid": v(101.25, -174.54) * mm, "end": v(103.82, -173.47) * mm});
            skArc(sketch, "E689", {"start": v(103.82, -173.47) * mm, "mid": v(104.95, -174.54) * mm, "end": v(106.1, -173.47) * mm});
            skArc(sketch, "E690", {"start": v(96.41, -173.47) * mm, "mid": v(97.55, -174.54) * mm, "end": v(98.69, -173.47) * mm});
            skLineSegment(sketch, "E691", {"start": v(99.24, -157.29) * mm, "end": v(99.24, -152.35) * mm});
            skLineSegment(sketch, "E692", {"start": v(103.26, -157.29) * mm, "end": v(103.26, -152.35) * mm});
            skLineSegment(sketch, "E693", {"start": v(101.25, -151.19) * mm, "end": v(99.24, -152.35) * mm});
            skLineSegment(sketch, "E694", {"start": v(101.25, -151.19) * mm, "end": v(103.26, -152.35) * mm});
            skLineSegment(sketch, "E695", {"start": v(101.25, -151.19) * mm, "end": v(101.25, -153.73) * mm});
            skArc(sketch, "E696", {"start": v(101.25, -153.73) * mm, "mid": v(101.84, -155.15) * mm, "end": v(103.26, -155.74) * mm});
            skLineSegment(sketch, "E697", {"start": v(-9.09, 41.6) * mm, "end": v(-12.13, 41.6) * mm});
            skLineSegment(sketch, "E698", {"start": v(-12.13, 41.6) * mm, "end": v(-12.13, 56.84) * mm});
            skLineSegment(sketch, "E699", {"start": v(-9.09, 41.6) * mm, "end": v(-9.09, 56.84) * mm});
            skArc(sketch, "E700", {"start": v(-8.32, 57.6) * mm, "mid": v(-8.86, 57.38) * mm, "end": v(-9.09, 56.84) * mm});
            skArc(sketch, "E701", {"start": v(-8.32, 60.65) * mm, "mid": v(-11.02, 59.53) * mm, "end": v(-12.13, 56.84) * mm});
            skLineSegment(sketch, "E702", {"start": v(-8.32, 60.65) * mm, "end": v(40.73, 60.65) * mm});
            skLineSegment(sketch, "E703", {"start": v(-8.32, 57.6) * mm, "end": v(40.73, 57.6) * mm});
            skArc(sketch, "E704", {"start": v(41.5, 56.84) * mm, "mid": v(41.27, 57.38) * mm, "end": v(40.73, 57.6) * mm});
            skArc(sketch, "E705", {"start": v(44.54, 56.84) * mm, "mid": v(43.43, 59.53) * mm, "end": v(40.73, 60.65) * mm});
            skLineSegment(sketch, "E706", {"start": v(44.54, 56.84) * mm, "end": v(44.54, -75.94) * mm});
            skLineSegment(sketch, "E707", {"start": v(41.5, 56.84) * mm, "end": v(41.5, -75.94) * mm});
            skLineSegment(sketch, "E708", {"start": v(98.81, 41.6) * mm, "end": v(101.86, 41.6) * mm});
            skLineSegment(sketch, "E709", {"start": v(101.86, 41.6) * mm, "end": v(101.86, 56.84) * mm});
            skLineSegment(sketch, "E710", {"start": v(98.81, 41.6) * mm, "end": v(98.81, 56.84) * mm});
            skArc(sketch, "E711", {"start": v(98.81, 56.84) * mm, "mid": v(98.59, 57.38) * mm, "end": v(98.05, 57.6) * mm});
            skArc(sketch, "E712", {"start": v(101.86, 56.84) * mm, "mid": v(100.74, 59.53) * mm, "end": v(98.05, 60.65) * mm});
            skLineSegment(sketch, "E713", {"start": v(98.05, 60.65) * mm, "end": v(49, 60.65) * mm});
            skLineSegment(sketch, "E714", {"start": v(98.05, 57.6) * mm, "end": v(49, 57.6) * mm});
            skArc(sketch, "E715", {"start": v(49, 57.6) * mm, "mid": v(48.45, 57.38) * mm, "end": v(48.23, 56.84) * mm});
            skArc(sketch, "E716", {"start": v(49, 60.65) * mm, "mid": v(46.3, 59.53) * mm, "end": v(45.18, 56.84) * mm});
            skLineSegment(sketch, "E717", {"start": v(45.18, 56.84) * mm, "end": v(45.18, -75.94) * mm});
            skLineSegment(sketch, "E718", {"start": v(48.23, 56.84) * mm, "end": v(48.23, -75.94) * mm});
            skLineSegment(sketch, "E719", {"start": v(83.37, -136.63) * mm, "end": v(83.37, -135.36) * mm});
            skLineSegment(sketch, "E720", {"start": v(70.16, -136.63) * mm, "end": v(70.16, -135.36) * mm});
            skLineSegment(sketch, "E721", {"start": v(81.96, -141.05) * mm, "end": v(81.96, -136.63) * mm});
            skLineSegment(sketch, "E722", {"start": v(71.57, -141.05) * mm, "end": v(71.57, -136.63) * mm});
            skLineSegment(sketch, "E723", {"start": v(79.2, -93.54) * mm, "end": v(79.2, -92.52) * mm});
            skLineSegment(sketch, "E724", {"start": v(79.2, -91.73) * mm, "end": v(79.2, -90.7) * mm});
            skLineSegment(sketch, "E725", {"start": v(79.2, -89.92) * mm, "end": v(79.2, -88.9) * mm});
            skLineSegment(sketch, "E726", {"start": v(79.2, -88.1) * mm, "end": v(79.2, -87.08) * mm});
            skLineSegment(sketch, "E727", {"start": v(79.2, -86.3) * mm, "end": v(79.2, -85.27) * mm});
            skLineSegment(sketch, "E728", {"start": v(79.2, -84.48) * mm, "end": v(79.2, -83.46) * mm});
            skLineSegment(sketch, "E729", {"start": v(79.2, -82.66) * mm, "end": v(79.2, -81.64) * mm});
            skLineSegment(sketch, "E730", {"start": v(79.2, -80.85) * mm, "end": v(79.2, -79.83) * mm});
            skLineSegment(sketch, "E731", {"start": v(79.2, -79.04) * mm, "end": v(79.2, -78.01) * mm});
            skLineSegment(sketch, "E732", {"start": v(79.2, -77.22) * mm, "end": v(79.2, -76.2) * mm});
            skLineSegment(sketch, "E733", {"start": v(79.2, -75.4) * mm, "end": v(79.2, -74.39) * mm});
            skLineSegment(sketch, "E734", {"start": v(74.32, -95.36) * mm, "end": v(74.32, -94.34) * mm});
            skLineSegment(sketch, "E735", {"start": v(74.32, -93.54) * mm, "end": v(74.32, -92.52) * mm});
            skLineSegment(sketch, "E736", {"start": v(74.32, -91.73) * mm, "end": v(74.32, -90.7) * mm});
            skLineSegment(sketch, "E737", {"start": v(74.32, -89.92) * mm, "end": v(74.32, -88.9) * mm});
            skLineSegment(sketch, "E738", {"start": v(74.32, -88.1) * mm, "end": v(74.32, -87.08) * mm});
            skLineSegment(sketch, "E739", {"start": v(74.32, -86.3) * mm, "end": v(74.32, -85.27) * mm});
            skLineSegment(sketch, "E740", {"start": v(74.32, -84.48) * mm, "end": v(74.32, -83.46) * mm});
            skLineSegment(sketch, "E741", {"start": v(74.32, -82.66) * mm, "end": v(74.32, -81.64) * mm});
            skLineSegment(sketch, "E742", {"start": v(74.32, -80.85) * mm, "end": v(74.32, -79.83) * mm});
            skLineSegment(sketch, "E743", {"start": v(74.32, -79.04) * mm, "end": v(74.32, -78.01) * mm});
            skLineSegment(sketch, "E744", {"start": v(74.32, -77.22) * mm, "end": v(74.32, -76.2) * mm});
            skLineSegment(sketch, "E745", {"start": v(73.64, -93.94) * mm, "end": v(74.32, -94.34) * mm});
            skLineSegment(sketch, "E746", {"start": v(73.64, -93.94) * mm, "end": v(74.32, -93.54) * mm});
            skLineSegment(sketch, "E747", {"start": v(73.64, -92.13) * mm, "end": v(74.32, -92.52) * mm});
            skLineSegment(sketch, "E748", {"start": v(73.64, -92.13) * mm, "end": v(74.32, -91.73) * mm});
            skLineSegment(sketch, "E749", {"start": v(79.89, -92.13) * mm, "end": v(79.2, -92.52) * mm});
            skLineSegment(sketch, "E750", {"start": v(79.89, -92.13) * mm, "end": v(79.2, -91.73) * mm});
            skLineSegment(sketch, "E751", {"start": v(79.89, -90.31) * mm, "end": v(79.2, -90.7) * mm});
            skLineSegment(sketch, "E752", {"start": v(79.89, -90.31) * mm, "end": v(79.2, -89.92) * mm});
            skLineSegment(sketch, "E753", {"start": v(73.64, -93.94) * mm, "end": v(79.89, -92.13) * mm});
            skLineSegment(sketch, "E754", {"start": v(73.64, -92.13) * mm, "end": v(79.89, -90.31) * mm});
            skLineSegment(sketch, "E755", {"start": v(74.32, -94.34) * mm, "end": v(79.2, -92.52) * mm});
            skLineSegment(sketch, "E756", {"start": v(74.32, -93.54) * mm, "end": v(79.2, -91.73) * mm});
            skLineSegment(sketch, "E757", {"start": v(74.32, -92.52) * mm, "end": v(79.2, -90.7) * mm});
            skLineSegment(sketch, "E758", {"start": v(74.32, -91.73) * mm, "end": v(79.2, -89.92) * mm});
            skLineSegment(sketch, "E759", {"start": v(73.64, -90.31) * mm, "end": v(74.32, -90.7) * mm});
            skLineSegment(sketch, "E760", {"start": v(73.64, -90.31) * mm, "end": v(74.32, -89.92) * mm});
            skLineSegment(sketch, "E761", {"start": v(73.64, -88.5) * mm, "end": v(74.32, -88.9) * mm});
            skLineSegment(sketch, "E762", {"start": v(73.64, -88.5) * mm, "end": v(74.32, -88.1) * mm});
            skLineSegment(sketch, "E763", {"start": v(79.89, -88.5) * mm, "end": v(79.2, -88.9) * mm});
            skLineSegment(sketch, "E764", {"start": v(79.89, -88.5) * mm, "end": v(79.2, -88.1) * mm});
            skLineSegment(sketch, "E765", {"start": v(79.89, -86.69) * mm, "end": v(79.2, -87.08) * mm});
            skLineSegment(sketch, "E766", {"start": v(79.89, -86.69) * mm, "end": v(79.2, -86.3) * mm});
            skLineSegment(sketch, "E767", {"start": v(73.64, -90.31) * mm, "end": v(79.89, -88.5) * mm});
            skLineSegment(sketch, "E768", {"start": v(73.64, -88.5) * mm, "end": v(79.89, -86.69) * mm});
            skLineSegment(sketch, "E769", {"start": v(74.32, -90.7) * mm, "end": v(79.2, -88.9) * mm});
            skLineSegment(sketch, "E770", {"start": v(74.32, -89.92) * mm, "end": v(79.2, -88.1) * mm});
            skLineSegment(sketch, "E771", {"start": v(74.32, -88.9) * mm, "end": v(79.2, -87.08) * mm});
            skLineSegment(sketch, "E772", {"start": v(74.32, -88.1) * mm, "end": v(79.2, -86.3) * mm});
            skLineSegment(sketch, "E773", {"start": v(73.64, -86.69) * mm, "end": v(74.32, -87.08) * mm});
            skLineSegment(sketch, "E774", {"start": v(73.64, -86.69) * mm, "end": v(74.32, -86.3) * mm});
            skLineSegment(sketch, "E775", {"start": v(79.89, -84.87) * mm, "end": v(79.2, -85.27) * mm});
            skLineSegment(sketch, "E776", {"start": v(79.89, -84.87) * mm, "end": v(79.2, -84.48) * mm});
            skLineSegment(sketch, "E777", {"start": v(73.64, -86.69) * mm, "end": v(79.89, -84.87) * mm});
            skLineSegment(sketch, "E778", {"start": v(74.32, -87.08) * mm, "end": v(79.2, -85.27) * mm});
            skLineSegment(sketch, "E779", {"start": v(74.32, -86.3) * mm, "end": v(79.2, -84.48) * mm});
            skLineSegment(sketch, "E780", {"start": v(73.64, -84.87) * mm, "end": v(74.32, -85.27) * mm});
            skLineSegment(sketch, "E781", {"start": v(73.64, -84.87) * mm, "end": v(74.32, -84.48) * mm});
            skLineSegment(sketch, "E782", {"start": v(73.64, -83.06) * mm, "end": v(74.32, -83.46) * mm});
            skLineSegment(sketch, "E783", {"start": v(73.64, -83.06) * mm, "end": v(74.32, -82.66) * mm});
            skLineSegment(sketch, "E784", {"start": v(79.89, -83.06) * mm, "end": v(79.2, -83.46) * mm});
            skLineSegment(sketch, "E785", {"start": v(79.89, -83.06) * mm, "end": v(79.2, -82.66) * mm});
            skLineSegment(sketch, "E786", {"start": v(79.89, -81.25) * mm, "end": v(79.2, -81.64) * mm});
            skLineSegment(sketch, "E787", {"start": v(79.89, -81.25) * mm, "end": v(79.2, -80.85) * mm});
            skLineSegment(sketch, "E788", {"start": v(73.64, -84.87) * mm, "end": v(79.89, -83.06) * mm});
            skLineSegment(sketch, "E789", {"start": v(73.64, -83.06) * mm, "end": v(79.89, -81.25) * mm});
            skLineSegment(sketch, "E790", {"start": v(74.32, -85.27) * mm, "end": v(79.2, -83.46) * mm});
            skLineSegment(sketch, "E791", {"start": v(74.32, -84.48) * mm, "end": v(79.2, -82.66) * mm});
            skLineSegment(sketch, "E792", {"start": v(74.32, -83.46) * mm, "end": v(79.2, -81.64) * mm});
            skLineSegment(sketch, "E793", {"start": v(74.32, -82.66) * mm, "end": v(79.2, -80.85) * mm});
            skLineSegment(sketch, "E794", {"start": v(73.64, -81.25) * mm, "end": v(74.32, -81.64) * mm});
            skLineSegment(sketch, "E795", {"start": v(73.64, -81.25) * mm, "end": v(74.32, -80.85) * mm});
            skLineSegment(sketch, "E796", {"start": v(73.64, -79.43) * mm, "end": v(74.32, -79.83) * mm});
            skLineSegment(sketch, "E797", {"start": v(73.64, -79.43) * mm, "end": v(74.32, -79.04) * mm});
            skLineSegment(sketch, "E798", {"start": v(79.89, -79.43) * mm, "end": v(79.2, -79.83) * mm});
            skLineSegment(sketch, "E799", {"start": v(79.89, -79.43) * mm, "end": v(79.2, -79.04) * mm});
            skLineSegment(sketch, "E800", {"start": v(79.89, -77.62) * mm, "end": v(79.2, -78.01) * mm});
            skLineSegment(sketch, "E801", {"start": v(79.89, -77.62) * mm, "end": v(79.2, -77.22) * mm});
            skLineSegment(sketch, "E802", {"start": v(73.64, -81.25) * mm, "end": v(79.89, -79.43) * mm});
            skLineSegment(sketch, "E803", {"start": v(73.64, -79.43) * mm, "end": v(79.89, -77.62) * mm});
            skLineSegment(sketch, "E804", {"start": v(74.32, -81.64) * mm, "end": v(79.2, -79.83) * mm});
            skLineSegment(sketch, "E805", {"start": v(74.32, -80.85) * mm, "end": v(79.2, -79.04) * mm});
            skLineSegment(sketch, "E806", {"start": v(74.32, -79.83) * mm, "end": v(79.2, -78.01) * mm});
            skLineSegment(sketch, "E807", {"start": v(74.32, -79.04) * mm, "end": v(79.2, -77.22) * mm});
            skLineSegment(sketch, "E808", {"start": v(73.64, -77.62) * mm, "end": v(74.32, -78.01) * mm});
            skLineSegment(sketch, "E809", {"start": v(73.64, -77.62) * mm, "end": v(74.32, -77.22) * mm});
            skLineSegment(sketch, "E810", {"start": v(73.64, -75.8) * mm, "end": v(74.32, -76.2) * mm});
            skLineSegment(sketch, "E811", {"start": v(73.64, -75.8) * mm, "end": v(74.32, -75.4) * mm});
            skLineSegment(sketch, "E812", {"start": v(79.89, -75.8) * mm, "end": v(79.2, -76.2) * mm});
            skLineSegment(sketch, "E813", {"start": v(79.89, -75.8) * mm, "end": v(79.2, -75.4) * mm});
            skLineSegment(sketch, "E814", {"start": v(79.89, -74) * mm, "end": v(79.2, -74.39) * mm});
            skLineSegment(sketch, "E815", {"start": v(79.89, -74) * mm, "end": v(79.2, -73.6) * mm});
            skLineSegment(sketch, "E816", {"start": v(73.64, -77.62) * mm, "end": v(79.89, -75.8) * mm});
            skLineSegment(sketch, "E817", {"start": v(73.64, -75.8) * mm, "end": v(79.89, -74) * mm});
            skLineSegment(sketch, "E818", {"start": v(74.32, -78.01) * mm, "end": v(79.2, -76.2) * mm});
            skLineSegment(sketch, "E819", {"start": v(74.32, -77.22) * mm, "end": v(79.2, -75.4) * mm});
            skLineSegment(sketch, "E820", {"start": v(74.32, -76.2) * mm, "end": v(79.2, -74.39) * mm});
            skLineSegment(sketch, "E821", {"start": v(74.32, -75.4) * mm, "end": v(79.2, -73.6) * mm});
            skLineSegment(sketch, "E822", {"start": v(70.16, -135.36) * mm, "end": v(83.37, -135.36) * mm});
            skLineSegment(sketch, "E823", {"start": v(70.16, -136.63) * mm, "end": v(83.37, -136.63) * mm});
            skLineSegment(sketch, "E824", {"start": v(72.26, -141.45) * mm, "end": v(81.26, -141.45) * mm});
            skLineSegment(sketch, "E825", {"start": v(74.16, -141.05) * mm, "end": v(74.16, -136.63) * mm});
            skLineSegment(sketch, "E826", {"start": v(79.36, -141.05) * mm, "end": v(79.36, -136.63) * mm});
            skLineSegment(sketch, "E827", {"start": v(72.26, -141.45) * mm, "end": v(71.57, -141.05) * mm});
            skLineSegment(sketch, "E828", {"start": v(81.26, -141.45) * mm, "end": v(81.96, -141.05) * mm});
            skLineSegment(sketch, "E829", {"start": v(78.66, -141.45) * mm, "end": v(79.36, -141.05) * mm});
            skLineSegment(sketch, "E830", {"start": v(73.47, -141.45) * mm, "end": v(74.16, -141.05) * mm});
            skLineSegment(sketch, "E831", {"start": v(80.05, -141.45) * mm, "end": v(79.36, -141.05) * mm});
            skLineSegment(sketch, "E832", {"start": v(74.86, -141.45) * mm, "end": v(74.16, -141.05) * mm});
            skLineSegment(sketch, "E833", {"start": v(74.32, -75.4) * mm, "end": v(74.32, -63.93) * mm});
            skLineSegment(sketch, "E834", {"start": v(78.55, -73.84) * mm, "end": v(78.55, -63.93) * mm});
            skLineSegment(sketch, "E835", {"start": v(76.44, -62.7) * mm, "end": v(74.32, -63.93) * mm});
            skLineSegment(sketch, "E836", {"start": v(76.44, -62.7) * mm, "end": v(78.55, -63.93) * mm});
            skLineSegment(sketch, "E837", {"start": v(76.44, -62.7) * mm, "end": v(76.44, -72.23) * mm});
            skArc(sketch, "E838", {"start": v(76.44, -72.23) * mm, "mid": v(76.77, -73.38) * mm, "end": v(77.68, -74.16) * mm});
            skLineSegment(sketch, "E839", {"start": v(73.64, -95.75) * mm, "end": v(74.32, -96.15) * mm});
            skLineSegment(sketch, "E840", {"start": v(73.64, -95.75) * mm, "end": v(74.32, -95.36) * mm});
            skLineSegment(sketch, "E841", {"start": v(79.89, -93.94) * mm, "end": v(79.2, -94.34) * mm});
            skLineSegment(sketch, "E842", {"start": v(79.89, -93.94) * mm, "end": v(79.2, -93.54) * mm});
            skLineSegment(sketch, "E843", {"start": v(73.64, -95.75) * mm, "end": v(79.89, -93.94) * mm});
            skLineSegment(sketch, "E844", {"start": v(74.32, -96.15) * mm, "end": v(79.2, -94.34) * mm});
            skLineSegment(sketch, "E845", {"start": v(74.32, -95.36) * mm, "end": v(79.2, -93.54) * mm});
            skLineSegment(sketch, "E846", {"start": v(74.32, -96.15) * mm, "end": v(74.32, -135.36) * mm});
            skLineSegment(sketch, "E847", {"start": v(79.2, -94.34) * mm, "end": v(79.2, -135.36) * mm});
            skSolve(sketch);
        }
        {
            var Q0;
            {var subQ1=sQuery(id+"F0.wireOp",EDGE,"E564");Q0=makeQuery(id+"F0.imprint","IMPRINT",FACE,{"disambiguationData":[TD([[makeQuery(id+"F0.imprint","IMPRINT",EDGE,{"derivedFrom":subQ1}),1.0]])]});}
            var Q1;
            Q1=makeQuery(id+"F0.imprint","IMPRINT",FACE,{"disambiguationData":[TD([[makeQuery(id+"F0.imprint","IMPRINT",EDGE,{"derivedFrom":sQuery(id+"F0.wireOp",EDGE,"E405")}),1.0]])]});
            var Q2;
            {var subQ0=sQuery(id+"F0.wireOp",EDGE,"E568");Q2=makeQuery(id+"F0.imprint","IMPRINT",FACE,{"disambiguationData":[TD([[makeQuery(id+"F0.imprint","IMPRINT",EDGE,{"derivedFrom":subQ0}),1.0]])]});}
            extrude(context, id + "F1", {"entities" : qUnion([Q0, Q1, Q2]), "depth" : 2413 * mm, "offsetDistance" : 25.4 * mm});
        }
    });
